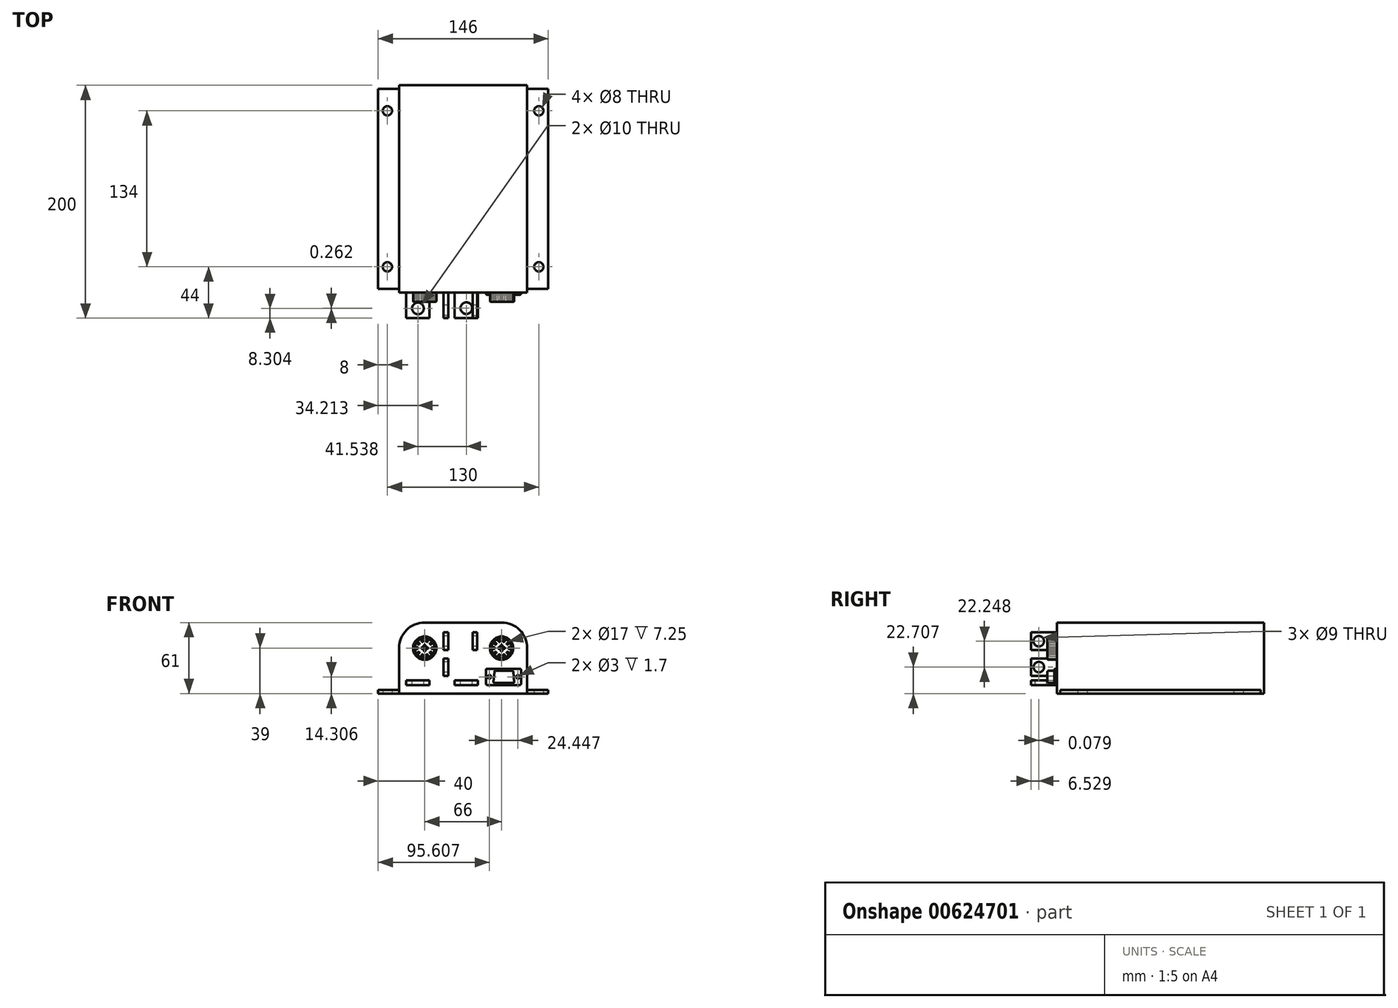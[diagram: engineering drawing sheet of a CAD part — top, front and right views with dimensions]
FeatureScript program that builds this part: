
annotation { "Feature Type Name" : "Feature", "Feature Type Description" : "" }
export const myFeature = defineFeature(function(context is Context, id is Id, definition is map)
    precondition{}
    {
        {
            var Q0;
            Q0=qCreatedBy(makeId("Top.planeOp"),FACE);
            var sketch = newSketch(context, id + "F0", { "sketchPlane" : qUnion([Q0])});
            skLineSegment(sketch, "E0.bottom", {"start": v(73, -86) * mm, "end": v(-73, -86) * mm});
            skLineSegment(sketch, "E0.top", {"start": v(73, 86) * mm, "end": v(-73, 86) * mm});
            skLineSegment(sketch, "E0.left", {"start": v(73, -86) * mm, "end": v(73, 86) * mm});
            skLineSegment(sketch, "E0.right", {"start": v(-73, -86) * mm, "end": v(-73, 86) * mm});
            skPoint(sketch, "E0.middle", {"position": v(0, 0) * mm});
            skLineSegment(sketch, "E1.bottom", {"start": v(65, -67) * mm, "end": v(-65, -67) * mm});
            skLineSegment(sketch, "E1.top", {"start": v(65, 67) * mm, "end": v(-65, 67) * mm});
            skLineSegment(sketch, "E1.left", {"start": v(65, -67) * mm, "end": v(65, 67) * mm});
            skLineSegment(sketch, "E1.right", {"start": v(-65, -67) * mm, "end": v(-65, 67) * mm});
            skLineSegment(sketch, "E2.bottom", {"start": v(55, -89) * mm, "end": v(-55, -89) * mm});
            skLineSegment(sketch, "E2.top", {"start": v(55, 89) * mm, "end": v(-55, 89) * mm});
            skLineSegment(sketch, "E2.left", {"start": v(55, -89) * mm, "end": v(55, 89) * mm});
            skLineSegment(sketch, "E2.right", {"start": v(-55, -89) * mm, "end": v(-55, 89) * mm});
            skCircle(sketch, "E3", {"center": v(-65, 67) * mm, "radius": 4 * mm});
            skCircle(sketch, "E4", {"center": v(65, 67) * mm, "radius": 4 * mm});
            skCircle(sketch, "E5", {"center": v(-65, -67) * mm, "radius": 4 * mm});
            skCircle(sketch, "E6", {"center": v(65, -67) * mm, "radius": 4 * mm});
            skSolve(sketch);
        }
        {
            var Q0;
            {var subQ5=sQuery(id+"F0.wireOp",EDGE,"E2.top");Q0=makeQuery(id+"F0.imprint","IMPRINT",FACE,{"disambiguationData":[TD([[makeQuery(id+"F0.imprint","IMPRINT",EDGE,{"derivedFrom":subQ5}),1.0]])]});}
            var Q1;
            {var subQ0=sQuery(id+"F0.wireOp",EDGE,"E2.left");var subQ1=sQuery(id+"F0.wireOp",EDGE,"E0.top");var subQ2=makeQuery(id+"F0.imprint","INTERSECT",VERTEX,{"derivedFrom":[subQ1,subQ0]});Q1=makeQuery(id+"F0.imprint","IMPRINT",FACE,{"disambiguationData":[TD([[makeQuery(id+"F0.imprint","IMPRINT",EDGE,{"disambiguationData":[TD([[subQ2,-1.0]])],"derivedFrom":subQ1}),1.0]])]});}
            var Q2;
            {var subQ0=sQuery(id+"F0.wireOp",EDGE,"E2.left");var subQ1=sQuery(id+"F0.wireOp",EDGE,"E1.bottom");var subQ2=makeQuery(id+"F0.imprint","INTERSECT",VERTEX,{"derivedFrom":[subQ1,subQ0]});Q2=makeQuery(id+"F0.imprint","IMPRINT",FACE,{"disambiguationData":[TD([[makeQuery(id+"F0.imprint","IMPRINT",EDGE,{"disambiguationData":[TD([[subQ2,-1.0]])],"derivedFrom":subQ1}),-1.0]])]});}
            var Q3;
            {var subQ0=sQuery(id+"F0.wireOp",EDGE,"E2.left");var subQ1=sQuery(id+"F0.wireOp",EDGE,"E0.bottom");var subQ2=makeQuery(id+"F0.imprint","INTERSECT",VERTEX,{"derivedFrom":[subQ1,subQ0]});Q3=makeQuery(id+"F0.imprint","IMPRINT",FACE,{"disambiguationData":[TD([[makeQuery(id+"F0.imprint","IMPRINT",EDGE,{"disambiguationData":[TD([[subQ2,-1.0]])],"derivedFrom":subQ1}),-1.0]])]});}
            var Q4;
            {var subQ5=sQuery(id+"F0.wireOp",EDGE,"E2.bottom");Q4=makeQuery(id+"F0.imprint","IMPRINT",FACE,{"disambiguationData":[TD([[makeQuery(id+"F0.imprint","IMPRINT",EDGE,{"derivedFrom":subQ5}),-1.0]])]});}
            extrude(context, id + "F1", {"entities" : qUnion([Q0, Q1, Q2, Q3, Q4]), "depth" : 61 * mm, "offsetDistance" : 25 * mm});
        }
        {
            var Q0;
            {var subQ9=sQuery(id+"F0.wireOp",EDGE,"E0.right");Q0=makeQuery(id+"F0.imprint","IMPRINT",FACE,{"disambiguationData":[TD([[makeQuery(id+"F0.imprint","IMPRINT",EDGE,{"derivedFrom":subQ9}),-1.0]])]});}
            var Q1;
            {var subQ0=sQuery(id+"F0.wireOp",EDGE,"E2.right");var subQ1=sQuery(id+"F0.wireOp",EDGE,"E1.bottom");var subQ2=makeQuery(id+"F0.imprint","INTERSECT",VERTEX,{"derivedFrom":[subQ1,subQ0]});Q1=makeQuery(id+"F0.imprint","IMPRINT",FACE,{"disambiguationData":[TD([[makeQuery(id+"F0.imprint","IMPRINT",EDGE,{"disambiguationData":[TD([[subQ2,-1.0]])],"derivedFrom":subQ1}),-1.0]])]});}
            var Q2;
            {var subQ5=sQuery(id+"F0.wireOp",EDGE,"E2.top");Q2=makeQuery(id+"F0.imprint","IMPRINT",FACE,{"disambiguationData":[TD([[makeQuery(id+"F0.imprint","IMPRINT",EDGE,{"derivedFrom":subQ5}),1.0]])]});}
            var Q3;
            {var subQ0=sQuery(id+"F0.wireOp",EDGE,"E2.left");var subQ1=sQuery(id+"F0.wireOp",EDGE,"E0.top");var subQ2=makeQuery(id+"F0.imprint","INTERSECT",VERTEX,{"derivedFrom":[subQ1,subQ0]});Q3=makeQuery(id+"F0.imprint","IMPRINT",FACE,{"disambiguationData":[TD([[makeQuery(id+"F0.imprint","IMPRINT",EDGE,{"disambiguationData":[TD([[subQ2,-1.0]])],"derivedFrom":subQ1}),1.0]])]});}
            var Q4;
            {var subQ0=sQuery(id+"F0.wireOp",EDGE,"E2.left");var subQ1=sQuery(id+"F0.wireOp",EDGE,"E1.bottom");var subQ2=makeQuery(id+"F0.imprint","INTERSECT",VERTEX,{"derivedFrom":[subQ1,subQ0]});Q4=makeQuery(id+"F0.imprint","IMPRINT",FACE,{"disambiguationData":[TD([[makeQuery(id+"F0.imprint","IMPRINT",EDGE,{"disambiguationData":[TD([[subQ2,-1.0]])],"derivedFrom":subQ1}),-1.0]])]});}
            var Q5;
            {var subQ0=sQuery(id+"F0.wireOp",EDGE,"E2.left");var subQ1=sQuery(id+"F0.wireOp",EDGE,"E0.bottom");var subQ2=makeQuery(id+"F0.imprint","INTERSECT",VERTEX,{"derivedFrom":[subQ1,subQ0]});Q5=makeQuery(id+"F0.imprint","IMPRINT",FACE,{"disambiguationData":[TD([[makeQuery(id+"F0.imprint","IMPRINT",EDGE,{"disambiguationData":[TD([[subQ2,-1.0]])],"derivedFrom":subQ1}),-1.0]])]});}
            var Q6;
            {var subQ5=sQuery(id+"F0.wireOp",EDGE,"E2.bottom");Q6=makeQuery(id+"F0.imprint","IMPRINT",FACE,{"disambiguationData":[TD([[makeQuery(id+"F0.imprint","IMPRINT",EDGE,{"derivedFrom":subQ5}),-1.0]])]});}
            var Q7;
            {var subQ1=sQuery(id+"F0.wireOp",EDGE,"E1.bottom");var subQ5=sQuery(id+"F0.wireOp",EDGE,"E6");var subQ11=makeQuery(id+"F0.imprint","INTERSECT",VERTEX,{"derivedFrom":[subQ1,subQ5]});Q7=makeQuery(id+"F0.imprint","IMPRINT",FACE,{"disambiguationData":[TD([[makeQuery(id+"F0.imprint","IMPRINT",EDGE,{"disambiguationData":[TD([[subQ11,-1.0]])],"derivedFrom":subQ1}),-1.0]])]});}
            var Q8;
            {var subQ5=sQuery(id+"F0.wireOp",EDGE,"E0.left");Q8=makeQuery(id+"F0.imprint","IMPRINT",FACE,{"disambiguationData":[TD([[makeQuery(id+"F0.imprint","IMPRINT",EDGE,{"derivedFrom":subQ5}),1.0]])]});}
            extrude(context, id + "F2", {"entities" : qUnion([Q0, Q1, Q2, Q3, Q4, Q5, Q6, Q7, Q8]), "operationType" : NewBodyOperationType.ADD, "depth" : 3 * mm, "offsetDistance" : 25 * mm});
        }
        {
            var Q0;
            Q0=makeQuery(id+"F1.opExtrude","CAP_EDGE",EDGE,{"disambiguationData":[OSD([sQuery(id+"F0.wireOp",EDGE,"E2.right")])],"isStart":false});
            var Q1;
            Q1=makeQuery(id+"F1.opExtrude","CAP_EDGE",EDGE,{"disambiguationData":[OSD([sQuery(id+"F0.wireOp",EDGE,"E2.left")])],"isStart":false});
            fillet(context, id + "F3", {"entities" : qUnion([Q0, Q1]), "radius" : 22 * mm, "tangentPropagation" : true, "allowEdgeOverflow" : false});
        }
        {
            var Q0;
            Q0=makeQuery(id+"F1.opExtrude","SWEPT_FACE",FACE,{"disambiguationData":[OSD([sQuery(id+"F0.wireOp",EDGE,"E2.bottom")])]});
            var sketch = newSketch(context, id + "F4", { "sketchPlane" : qUnion([Q0])});
            skCircle(sketch, "E7", {"center": v(33, 39) * mm, "radius": 10 * mm});
            skCircle(sketch, "E8", {"center": v(-33, 39) * mm, "radius": 10 * mm});
            skCircle(sketch, "E9", {"center": v(-33, 39) * mm, "radius": 8.5 * mm});
            skCircle(sketch, "E10", {"center": v(33, 39) * mm, "radius": 8.5 * mm});
            skCircle(sketch, "E11", {"center": v(-33, 39) * mm, "radius": 6.5 * mm});
            skCircle(sketch, "E12", {"center": v(33, 39) * mm, "radius": 6.5 * mm});
            skCircle(sketch, "E13.cCircle", {"center": v(-33, 39) * mm, "radius": 6.5 * mm, "construction": true});
            skLineSegment(sketch, "E13.0", {"start": v(-26.5, 39) * mm, "end": v(-27.74, 35.18) * mm});
            skLineSegment(sketch, "E13.1", {"start": v(-27.74, 35.18) * mm, "end": v(-31, 32.82) * mm});
            skLineSegment(sketch, "E13.2", {"start": v(-31, 32.82) * mm, "end": v(-35, 32.82) * mm});
            skLineSegment(sketch, "E13.3", {"start": v(-35, 32.82) * mm, "end": v(-38.26, 35.18) * mm});
            skLineSegment(sketch, "E13.4", {"start": v(-38.26, 35.18) * mm, "end": v(-39.5, 39) * mm});
            skLineSegment(sketch, "E13.5", {"start": v(-39.5, 39) * mm, "end": v(-38.26, 42.82) * mm});
            skLineSegment(sketch, "E13.6", {"start": v(-38.26, 42.82) * mm, "end": v(-35, 45.18) * mm});
            skLineSegment(sketch, "E13.7", {"start": v(-35, 45.18) * mm, "end": v(-31, 45.18) * mm});
            skLineSegment(sketch, "E13.8", {"start": v(-31, 45.18) * mm, "end": v(-27.74, 42.82) * mm});
            skLineSegment(sketch, "E13.9", {"start": v(-27.74, 42.82) * mm, "end": v(-26.5, 39) * mm});
            skCircle(sketch, "E14", {"center": v(-35, 45.18) * mm, "radius": 0.75 * mm});
            skCircle(sketch, "E15", {"center": v(-38.26, 42.82) * mm, "radius": 0.75 * mm});
            skCircle(sketch, "E16", {"center": v(-39.5, 39) * mm, "radius": 0.75 * mm});
            skCircle(sketch, "E17", {"center": v(-38.26, 35.18) * mm, "radius": 0.75 * mm});
            skCircle(sketch, "E18", {"center": v(-35, 32.82) * mm, "radius": 0.75 * mm});
            skCircle(sketch, "E19", {"center": v(-31, 32.82) * mm, "radius": 0.75 * mm});
            skCircle(sketch, "E20", {"center": v(-27.74, 35.18) * mm, "radius": 0.75 * mm});
            skCircle(sketch, "E21", {"center": v(-26.5, 39) * mm, "radius": 0.75 * mm});
            skCircle(sketch, "E22", {"center": v(-27.74, 42.82) * mm, "radius": 0.75 * mm});
            skCircle(sketch, "E23", {"center": v(-31, 45.18) * mm, "radius": 0.75 * mm});
            skCircle(sketch, "E24.cCircle", {"center": v(-33, 39) * mm, "radius": 2.12 * mm, "construction": true});
            skLineSegment(sketch, "E24.0", {"start": v(-30.88, 39) * mm, "end": v(-33, 36.88) * mm});
            skLineSegment(sketch, "E24.1", {"start": v(-33, 36.88) * mm, "end": v(-35.12, 39) * mm});
            skLineSegment(sketch, "E24.2", {"start": v(-35.12, 39) * mm, "end": v(-33, 41.12) * mm});
            skLineSegment(sketch, "E24.3", {"start": v(-33, 41.12) * mm, "end": v(-30.88, 39) * mm});
            skCircle(sketch, "E25", {"center": v(-33, 36.88) * mm, "radius": 0.75 * mm});
            skCircle(sketch, "E26", {"center": v(-33, 41.12) * mm, "radius": 0.75 * mm});
            skCircle(sketch, "E27", {"center": v(-30.88, 39) * mm, "radius": 0.75 * mm});
            skCircle(sketch, "E28", {"center": v(-35.12, 39) * mm, "radius": 0.75 * mm});
            skCircle(sketch, "E29.cCircle", {"center": v(33, 39) * mm, "radius": 6.5 * mm, "construction": true});
            skLineSegment(sketch, "E29.0", {"start": v(39.5, 39) * mm, "end": v(38.26, 35.18) * mm});
            skLineSegment(sketch, "E29.1", {"start": v(38.26, 35.18) * mm, "end": v(35, 32.82) * mm});
            skLineSegment(sketch, "E29.2", {"start": v(35, 32.82) * mm, "end": v(31, 32.82) * mm});
            skLineSegment(sketch, "E29.3", {"start": v(31, 32.82) * mm, "end": v(27.74, 35.18) * mm});
            skLineSegment(sketch, "E29.4", {"start": v(27.74, 35.18) * mm, "end": v(26.5, 39) * mm});
            skLineSegment(sketch, "E29.5", {"start": v(26.5, 39) * mm, "end": v(27.74, 42.82) * mm});
            skLineSegment(sketch, "E29.6", {"start": v(27.74, 42.82) * mm, "end": v(31, 45.18) * mm});
            skLineSegment(sketch, "E29.7", {"start": v(31, 45.18) * mm, "end": v(35, 45.18) * mm});
            skLineSegment(sketch, "E29.8", {"start": v(35, 45.18) * mm, "end": v(38.26, 42.82) * mm});
            skLineSegment(sketch, "E29.9", {"start": v(38.26, 42.82) * mm, "end": v(39.5, 39) * mm});
            skCircle(sketch, "E30", {"center": v(31, 45.18) * mm, "radius": 0.75 * mm});
            skCircle(sketch, "E31", {"center": v(27.74, 42.82) * mm, "radius": 0.75 * mm});
            skCircle(sketch, "E32", {"center": v(26.5, 39) * mm, "radius": 0.75 * mm});
            skCircle(sketch, "E33", {"center": v(27.74, 35.18) * mm, "radius": 0.75 * mm});
            skCircle(sketch, "E34", {"center": v(31, 32.82) * mm, "radius": 0.75 * mm});
            skCircle(sketch, "E35", {"center": v(35, 32.82) * mm, "radius": 0.75 * mm});
            skCircle(sketch, "E36", {"center": v(38.26, 35.18) * mm, "radius": 0.75 * mm});
            skCircle(sketch, "E37", {"center": v(39.5, 39) * mm, "radius": 0.75 * mm});
            skCircle(sketch, "E38", {"center": v(38.26, 42.82) * mm, "radius": 0.75 * mm});
            skCircle(sketch, "E39", {"center": v(35, 45.18) * mm, "radius": 0.75 * mm});
            skCircle(sketch, "E40.cCircle", {"center": v(33, 39) * mm, "radius": 2.12 * mm, "construction": true});
            skLineSegment(sketch, "E40.0", {"start": v(35.12, 39) * mm, "end": v(33, 36.88) * mm});
            skLineSegment(sketch, "E40.1", {"start": v(33, 36.88) * mm, "end": v(30.88, 39) * mm});
            skLineSegment(sketch, "E40.2", {"start": v(30.88, 39) * mm, "end": v(33, 41.12) * mm});
            skLineSegment(sketch, "E40.3", {"start": v(33, 41.12) * mm, "end": v(35.12, 39) * mm});
            skCircle(sketch, "E41", {"center": v(33, 36.88) * mm, "radius": 0.75 * mm});
            skCircle(sketch, "E42", {"center": v(33, 41.12) * mm, "radius": 0.75 * mm});
            skCircle(sketch, "E43", {"center": v(35.12, 39) * mm, "radius": 0.75 * mm});
            skCircle(sketch, "E44", {"center": v(30.88, 39) * mm, "radius": 0.75 * mm});
            skLineSegment(sketch, "E45.bottom", {"start": v(-48.79, 11.3) * mm, "end": v(-28.79, 11.3) * mm});
            skLineSegment(sketch, "E45.top", {"start": v(-48.79, 7.3) * mm, "end": v(-28.79, 7.3) * mm});
            skLineSegment(sketch, "E45.left", {"start": v(-48.79, 11.3) * mm, "end": v(-48.79, 7.3) * mm});
            skLineSegment(sketch, "E45.right", {"start": v(-28.79, 11.3) * mm, "end": v(-28.79, 7.3) * mm});
            skLineSegment(sketch, "E46.bottom", {"start": v(-16.77, 52.46) * mm, "end": v(-12.77, 52.46) * mm});
            skLineSegment(sketch, "E46.top", {"start": v(-16.77, 37.46) * mm, "end": v(-12.77, 37.46) * mm});
            skLineSegment(sketch, "E46.left", {"start": v(-16.77, 52.46) * mm, "end": v(-16.77, 37.46) * mm});
            skLineSegment(sketch, "E46.right", {"start": v(-12.77, 52.46) * mm, "end": v(-12.77, 37.46) * mm});
            skLineSegment(sketch, "E47.bottom", {"start": v(8.11, 52.46) * mm, "end": v(12.11, 52.46) * mm});
            skLineSegment(sketch, "E47.top", {"start": v(8.11, 37.46) * mm, "end": v(12.11, 37.46) * mm});
            skLineSegment(sketch, "E47.left", {"start": v(8.11, 52.46) * mm, "end": v(8.11, 37.46) * mm});
            skLineSegment(sketch, "E47.right", {"start": v(12.11, 52.46) * mm, "end": v(12.11, 37.46) * mm});
            skLineSegment(sketch, "E48.bottom", {"start": v(-16.77, 30.2) * mm, "end": v(-12.77, 30.2) * mm});
            skLineSegment(sketch, "E48.top", {"start": v(-16.77, 15.2) * mm, "end": v(-12.77, 15.2) * mm});
            skLineSegment(sketch, "E48.left", {"start": v(-16.77, 30.2) * mm, "end": v(-16.77, 15.2) * mm});
            skLineSegment(sketch, "E48.right", {"start": v(-12.77, 30.2) * mm, "end": v(-12.77, 15.2) * mm});
            skLineSegment(sketch, "E49.bottom", {"start": v(-7.25, 11.3) * mm, "end": v(12.75, 11.3) * mm});
            skLineSegment(sketch, "E49.top", {"start": v(-7.25, 7.3) * mm, "end": v(12.75, 7.3) * mm});
            skLineSegment(sketch, "E49.left", {"start": v(-7.25, 11.3) * mm, "end": v(-7.25, 7.3) * mm});
            skLineSegment(sketch, "E49.right", {"start": v(12.75, 11.3) * mm, "end": v(12.75, 7.3) * mm});
            skLineSegment(sketch, "E50.bottom", {"start": v(19.69, 7.3) * mm, "end": v(49.69, 7.3) * mm});
            skLineSegment(sketch, "E50.top", {"start": v(19.69, 21.3) * mm, "end": v(49.69, 21.3) * mm});
            skLineSegment(sketch, "E50.left", {"start": v(19.69, 7.3) * mm, "end": v(19.69, 21.3) * mm});
            skLineSegment(sketch, "E50.right", {"start": v(49.69, 7.3) * mm, "end": v(49.69, 21.3) * mm});
            skLineSegment(sketch, "E51", {"start": v(26.94, 19.6) * mm, "end": v(42.94, 19.6) * mm});
            skLineSegment(sketch, "E52", {"start": v(26.03, 9) * mm, "end": v(44.03, 9) * mm});
            skLineSegment(sketch, "E53", {"start": v(26.94, 19.6) * mm, "end": v(26.03, 9) * mm});
            skLineSegment(sketch, "E54", {"start": v(42.94, 19.6) * mm, "end": v(44.03, 9) * mm});
            skCircle(sketch, "E55", {"center": v(22.6, 14.3) * mm, "radius": 1.5 * mm});
            skPoint(sketch, "E55.centerSnap0", {"position": v(19.69, 14.3) * mm});
            skCircle(sketch, "E56", {"center": v(47.05, 14.3) * mm, "radius": 1.5 * mm});
            skPoint(sketch, "E56.centerSnap0", {"position": v(49.69, 14.3) * mm});
            skSolve(sketch);
        }
        {
            var Q0;
            {var subQ0=sQuery(id+"F4.wireOp",EDGE,"E11");var subQ2=sQuery(id+"F4.wireOp",EDGE,"E18");var subQ3=makeQuery(id+"F4.imprint","INTERSECT",VERTEX,{"disambiguationData":[OD(0.0)],"derivedFrom":[subQ0,subQ2]});Q0=makeQuery(id+"F4.imprint","IMPRINT",FACE,{"disambiguationData":[TD([[makeQuery(id+"F4.imprint","IMPRINT",EDGE,{"disambiguationData":[TD([[subQ3,-1.0]])],"derivedFrom":subQ2}),1.0]])]});}
            var Q1;
            {var subQ1=sQuery(id+"F4.wireOp",EDGE,"E13.2");var subQ3=sQuery(id+"F4.wireOp",EDGE,"E18");var subQ4=makeQuery(id+"F4.imprint","INTERSECT",VERTEX,{"derivedFrom":[subQ1,subQ3]});Q1=makeQuery(id+"F4.imprint","IMPRINT",FACE,{"disambiguationData":[TD([[makeQuery(id+"F4.imprint","IMPRINT",EDGE,{"disambiguationData":[TD([[subQ4,-1.0]])],"derivedFrom":subQ3}),1.0]])]});}
            var Q2;
            {var subQ0=sQuery(id+"F4.wireOp",EDGE,"E11");var subQ2=sQuery(id+"F4.wireOp",EDGE,"E19");var subQ3=makeQuery(id+"F4.imprint","INTERSECT",VERTEX,{"disambiguationData":[OD(0.0)],"derivedFrom":[subQ0,subQ2]});Q2=makeQuery(id+"F4.imprint","IMPRINT",FACE,{"disambiguationData":[TD([[makeQuery(id+"F4.imprint","IMPRINT",EDGE,{"disambiguationData":[TD([[subQ3,-1.0]])],"derivedFrom":subQ2}),1.0]])]});}
            var Q3;
            {var subQ1=sQuery(id+"F4.wireOp",EDGE,"E13.1");var subQ3=sQuery(id+"F4.wireOp",EDGE,"E19");var subQ4=makeQuery(id+"F4.imprint","INTERSECT",VERTEX,{"derivedFrom":[subQ1,subQ3]});Q3=makeQuery(id+"F4.imprint","IMPRINT",FACE,{"disambiguationData":[TD([[makeQuery(id+"F4.imprint","IMPRINT",EDGE,{"disambiguationData":[TD([[subQ4,-1.0]])],"derivedFrom":subQ3}),1.0]])]});}
            var Q4;
            {var subQ1=sQuery(id+"F4.wireOp",EDGE,"E11");var subQ3=sQuery(id+"F4.wireOp",EDGE,"E19");var subQ4=makeQuery(id+"F4.imprint","INTERSECT",VERTEX,{"disambiguationData":[OD(1.0)],"derivedFrom":[subQ1,subQ3]});Q4=makeQuery(id+"F4.imprint","IMPRINT",FACE,{"disambiguationData":[TD([[makeQuery(id+"F4.imprint","IMPRINT",EDGE,{"disambiguationData":[TD([[subQ4,-1.0]])],"derivedFrom":subQ3}),1.0]])]});}
            var Q5;
            {var subQ1=sQuery(id+"F4.wireOp",EDGE,"E11");var subQ3=sQuery(id+"F4.wireOp",EDGE,"E19");var subQ4=makeQuery(id+"F4.imprint","INTERSECT",VERTEX,{"disambiguationData":[OD(0.0)],"derivedFrom":[subQ1,subQ3]});Q5=makeQuery(id+"F4.imprint","IMPRINT",FACE,{"disambiguationData":[TD([[makeQuery(id+"F4.imprint","IMPRINT",EDGE,{"disambiguationData":[TD([[subQ4,1.0]])],"derivedFrom":subQ3}),1.0]])]});}
            var Q6;
            {var subQ0=sQuery(id+"F4.wireOp",EDGE,"E24.2");var subQ1=sQuery(id+"F4.wireOp",EDGE,"E24.1");var subQ2=makeQuery(id+"F4.imprint","INTERSECT",VERTEX,{"derivedFrom":[subQ1,subQ0]});Q6=makeQuery(id+"F4.imprint","IMPRINT",FACE,{"disambiguationData":[TD([[makeQuery(id+"F4.imprint","IMPRINT",EDGE,{"disambiguationData":[TD([[subQ2,1.0]])],"derivedFrom":subQ1}),-1.0]])]});}
            var Q7;
            {var subQ0=sQuery(id+"F4.wireOp",EDGE,"E24.2");var subQ1=sQuery(id+"F4.wireOp",EDGE,"E24.1");var subQ2=makeQuery(id+"F4.imprint","INTERSECT",VERTEX,{"derivedFrom":[subQ1,subQ0]});Q7=makeQuery(id+"F4.imprint","IMPRINT",FACE,{"disambiguationData":[TD([[makeQuery(id+"F4.imprint","IMPRINT",EDGE,{"disambiguationData":[TD([[subQ2,1.0]])],"derivedFrom":subQ1}),1.0]])]});}
            var Q8;
            {var subQ0=sQuery(id+"F4.wireOp",EDGE,"E24.3");var subQ1=sQuery(id+"F4.wireOp",EDGE,"E24.2");var subQ2=makeQuery(id+"F4.imprint","INTERSECT",VERTEX,{"derivedFrom":[subQ1,subQ0]});Q8=makeQuery(id+"F4.imprint","IMPRINT",FACE,{"disambiguationData":[TD([[makeQuery(id+"F4.imprint","IMPRINT",EDGE,{"disambiguationData":[TD([[subQ2,1.0]])],"derivedFrom":subQ1}),1.0]])]});}
            var Q9;
            {var subQ0=sQuery(id+"F4.wireOp",EDGE,"E24.3");var subQ1=sQuery(id+"F4.wireOp",EDGE,"E24.2");var subQ2=makeQuery(id+"F4.imprint","INTERSECT",VERTEX,{"derivedFrom":[subQ1,subQ0]});Q9=makeQuery(id+"F4.imprint","IMPRINT",FACE,{"disambiguationData":[TD([[makeQuery(id+"F4.imprint","IMPRINT",EDGE,{"disambiguationData":[TD([[subQ2,1.0]])],"derivedFrom":subQ1}),-1.0]])]});}
            var Q10;
            {var subQ0=sQuery(id+"F4.wireOp",EDGE,"E24.3");var subQ1=sQuery(id+"F4.wireOp",EDGE,"E24.0");var subQ2=makeQuery(id+"F4.imprint","INTERSECT",VERTEX,{"derivedFrom":[subQ1,subQ0]});Q10=makeQuery(id+"F4.imprint","IMPRINT",FACE,{"disambiguationData":[TD([[makeQuery(id+"F4.imprint","IMPRINT",EDGE,{"disambiguationData":[TD([[subQ2,-1.0]])],"derivedFrom":subQ1}),1.0]])]});}
            var Q11;
            {var subQ0=sQuery(id+"F4.wireOp",EDGE,"E24.3");var subQ1=sQuery(id+"F4.wireOp",EDGE,"E24.0");var subQ2=makeQuery(id+"F4.imprint","INTERSECT",VERTEX,{"derivedFrom":[subQ1,subQ0]});Q11=makeQuery(id+"F4.imprint","IMPRINT",FACE,{"disambiguationData":[TD([[makeQuery(id+"F4.imprint","IMPRINT",EDGE,{"disambiguationData":[TD([[subQ2,-1.0]])],"derivedFrom":subQ1}),-1.0]])]});}
            var Q12;
            {var subQ0=sQuery(id+"F4.wireOp",EDGE,"E24.1");var subQ1=sQuery(id+"F4.wireOp",EDGE,"E24.0");var subQ2=makeQuery(id+"F4.imprint","INTERSECT",VERTEX,{"derivedFrom":[subQ1,subQ0]});Q12=makeQuery(id+"F4.imprint","IMPRINT",FACE,{"disambiguationData":[TD([[makeQuery(id+"F4.imprint","IMPRINT",EDGE,{"disambiguationData":[TD([[subQ2,1.0]])],"derivedFrom":subQ1}),1.0]])]});}
            var Q13;
            {var subQ0=sQuery(id+"F4.wireOp",EDGE,"E24.1");var subQ1=sQuery(id+"F4.wireOp",EDGE,"E24.0");var subQ2=makeQuery(id+"F4.imprint","INTERSECT",VERTEX,{"derivedFrom":[subQ1,subQ0]});Q13=makeQuery(id+"F4.imprint","IMPRINT",FACE,{"disambiguationData":[TD([[makeQuery(id+"F4.imprint","IMPRINT",EDGE,{"disambiguationData":[TD([[subQ2,1.0]])],"derivedFrom":subQ1}),-1.0]])]});}
            var Q14;
            {var subQ1=sQuery(id+"F4.wireOp",EDGE,"E13.0");var subQ3=sQuery(id+"F4.wireOp",EDGE,"E20");var subQ4=makeQuery(id+"F4.imprint","INTERSECT",VERTEX,{"derivedFrom":[subQ1,subQ3]});Q14=makeQuery(id+"F4.imprint","IMPRINT",FACE,{"disambiguationData":[TD([[makeQuery(id+"F4.imprint","IMPRINT",EDGE,{"disambiguationData":[TD([[subQ4,-1.0]])],"derivedFrom":subQ3}),1.0]])]});}
            var Q15;
            {var subQ0=sQuery(id+"F4.wireOp",EDGE,"E11");var subQ2=sQuery(id+"F4.wireOp",EDGE,"E21");var subQ3=makeQuery(id+"F4.imprint","INTERSECT",VERTEX,{"disambiguationData":[OD(0.0)],"derivedFrom":[subQ0,subQ2]});Q15=makeQuery(id+"F4.imprint","IMPRINT",FACE,{"disambiguationData":[TD([[makeQuery(id+"F4.imprint","IMPRINT",EDGE,{"disambiguationData":[TD([[subQ3,1.0]])],"derivedFrom":subQ2}),1.0]])]});}
            var Q16;
            {var subQ1=sQuery(id+"F4.wireOp",EDGE,"E13.0");var subQ3=sQuery(id+"F4.wireOp",EDGE,"E21");var subQ4=makeQuery(id+"F4.imprint","INTERSECT",VERTEX,{"derivedFrom":[subQ1,subQ3]});Q16=makeQuery(id+"F4.imprint","IMPRINT",FACE,{"disambiguationData":[TD([[makeQuery(id+"F4.imprint","IMPRINT",EDGE,{"disambiguationData":[TD([[subQ4,1.0]])],"derivedFrom":subQ3}),1.0]])]});}
            var Q17;
            {var subQ0=sQuery(id+"F4.wireOp",EDGE,"E11");var subQ2=sQuery(id+"F4.wireOp",EDGE,"E22");var subQ3=makeQuery(id+"F4.imprint","INTERSECT",VERTEX,{"disambiguationData":[OD(0.0)],"derivedFrom":[subQ0,subQ2]});Q17=makeQuery(id+"F4.imprint","IMPRINT",FACE,{"disambiguationData":[TD([[makeQuery(id+"F4.imprint","IMPRINT",EDGE,{"disambiguationData":[TD([[subQ3,-1.0]])],"derivedFrom":subQ2}),1.0]])]});}
            var Q18;
            {var subQ1=sQuery(id+"F4.wireOp",EDGE,"E13.8");var subQ3=sQuery(id+"F4.wireOp",EDGE,"E22");var subQ4=makeQuery(id+"F4.imprint","INTERSECT",VERTEX,{"derivedFrom":[subQ1,subQ3]});Q18=makeQuery(id+"F4.imprint","IMPRINT",FACE,{"disambiguationData":[TD([[makeQuery(id+"F4.imprint","IMPRINT",EDGE,{"disambiguationData":[TD([[subQ4,-1.0]])],"derivedFrom":subQ3}),1.0]])]});}
            var Q19;
            {var subQ0=sQuery(id+"F4.wireOp",EDGE,"E11");var subQ2=sQuery(id+"F4.wireOp",EDGE,"E23");var subQ3=makeQuery(id+"F4.imprint","INTERSECT",VERTEX,{"disambiguationData":[OD(0.0)],"derivedFrom":[subQ0,subQ2]});Q19=makeQuery(id+"F4.imprint","IMPRINT",FACE,{"disambiguationData":[TD([[makeQuery(id+"F4.imprint","IMPRINT",EDGE,{"disambiguationData":[TD([[subQ3,-1.0]])],"derivedFrom":subQ2}),1.0]])]});}
            var Q20;
            {var subQ1=sQuery(id+"F4.wireOp",EDGE,"E13.7");var subQ3=sQuery(id+"F4.wireOp",EDGE,"E23");var subQ4=makeQuery(id+"F4.imprint","INTERSECT",VERTEX,{"derivedFrom":[subQ1,subQ3]});Q20=makeQuery(id+"F4.imprint","IMPRINT",FACE,{"disambiguationData":[TD([[makeQuery(id+"F4.imprint","IMPRINT",EDGE,{"disambiguationData":[TD([[subQ4,-1.0]])],"derivedFrom":subQ3}),1.0]])]});}
            var Q21;
            {var subQ0=sQuery(id+"F4.wireOp",EDGE,"E11");var subQ2=sQuery(id+"F4.wireOp",EDGE,"E14");var subQ3=makeQuery(id+"F4.imprint","INTERSECT",VERTEX,{"disambiguationData":[OD(0.0)],"derivedFrom":[subQ0,subQ2]});Q21=makeQuery(id+"F4.imprint","IMPRINT",FACE,{"disambiguationData":[TD([[makeQuery(id+"F4.imprint","IMPRINT",EDGE,{"disambiguationData":[TD([[subQ3,-1.0]])],"derivedFrom":subQ2}),1.0]])]});}
            var Q22;
            {var subQ1=sQuery(id+"F4.wireOp",EDGE,"E13.6");var subQ3=sQuery(id+"F4.wireOp",EDGE,"E14");var subQ4=makeQuery(id+"F4.imprint","INTERSECT",VERTEX,{"derivedFrom":[subQ1,subQ3]});Q22=makeQuery(id+"F4.imprint","IMPRINT",FACE,{"disambiguationData":[TD([[makeQuery(id+"F4.imprint","IMPRINT",EDGE,{"disambiguationData":[TD([[subQ4,-1.0]])],"derivedFrom":subQ3}),1.0]])]});}
            var Q23;
            {var subQ0=sQuery(id+"F4.wireOp",EDGE,"E11");var subQ2=sQuery(id+"F4.wireOp",EDGE,"E15");var subQ3=makeQuery(id+"F4.imprint","INTERSECT",VERTEX,{"disambiguationData":[OD(0.0)],"derivedFrom":[subQ0,subQ2]});Q23=makeQuery(id+"F4.imprint","IMPRINT",FACE,{"disambiguationData":[TD([[makeQuery(id+"F4.imprint","IMPRINT",EDGE,{"disambiguationData":[TD([[subQ3,-1.0]])],"derivedFrom":subQ2}),1.0]])]});}
            var Q24;
            {var subQ1=sQuery(id+"F4.wireOp",EDGE,"E13.5");var subQ3=sQuery(id+"F4.wireOp",EDGE,"E15");var subQ4=makeQuery(id+"F4.imprint","INTERSECT",VERTEX,{"derivedFrom":[subQ1,subQ3]});Q24=makeQuery(id+"F4.imprint","IMPRINT",FACE,{"disambiguationData":[TD([[makeQuery(id+"F4.imprint","IMPRINT",EDGE,{"disambiguationData":[TD([[subQ4,-1.0]])],"derivedFrom":subQ3}),1.0]])]});}
            var Q25;
            {var subQ0=sQuery(id+"F4.wireOp",EDGE,"E11");var subQ2=sQuery(id+"F4.wireOp",EDGE,"E16");var subQ3=makeQuery(id+"F4.imprint","INTERSECT",VERTEX,{"disambiguationData":[OD(0.0)],"derivedFrom":[subQ0,subQ2]});Q25=makeQuery(id+"F4.imprint","IMPRINT",FACE,{"disambiguationData":[TD([[makeQuery(id+"F4.imprint","IMPRINT",EDGE,{"disambiguationData":[TD([[subQ3,-1.0]])],"derivedFrom":subQ2}),1.0]])]});}
            var Q26;
            {var subQ0=sQuery(id+"F4.wireOp",EDGE,"E11");var subQ2=sQuery(id+"F4.wireOp",EDGE,"E17");var subQ3=makeQuery(id+"F4.imprint","INTERSECT",VERTEX,{"disambiguationData":[OD(0.0)],"derivedFrom":[subQ0,subQ2]});Q26=makeQuery(id+"F4.imprint","IMPRINT",FACE,{"disambiguationData":[TD([[makeQuery(id+"F4.imprint","IMPRINT",EDGE,{"disambiguationData":[TD([[subQ3,-1.0]])],"derivedFrom":subQ2}),1.0]])]});}
            var Q27;
            {var subQ1=sQuery(id+"F4.wireOp",EDGE,"E13.3");var subQ3=sQuery(id+"F4.wireOp",EDGE,"E17");var subQ4=makeQuery(id+"F4.imprint","INTERSECT",VERTEX,{"derivedFrom":[subQ1,subQ3]});Q27=makeQuery(id+"F4.imprint","IMPRINT",FACE,{"disambiguationData":[TD([[makeQuery(id+"F4.imprint","IMPRINT",EDGE,{"disambiguationData":[TD([[subQ4,-1.0]])],"derivedFrom":subQ3}),1.0]])]});}
            var Q28;
            {var subQ1=sQuery(id+"F4.wireOp",EDGE,"E11");var subQ3=sQuery(id+"F4.wireOp",EDGE,"E14");var subQ4=makeQuery(id+"F4.imprint","INTERSECT",VERTEX,{"disambiguationData":[OD(0.0)],"derivedFrom":[subQ1,subQ3]});Q28=makeQuery(id+"F4.imprint","IMPRINT",FACE,{"disambiguationData":[TD([[makeQuery(id+"F4.imprint","IMPRINT",EDGE,{"disambiguationData":[TD([[subQ4,1.0]])],"derivedFrom":subQ3}),1.0]])]});}
            var Q29;
            {var subQ1=sQuery(id+"F4.wireOp",EDGE,"E11");var subQ3=sQuery(id+"F4.wireOp",EDGE,"E14");var subQ4=makeQuery(id+"F4.imprint","INTERSECT",VERTEX,{"disambiguationData":[OD(1.0)],"derivedFrom":[subQ1,subQ3]});Q29=makeQuery(id+"F4.imprint","IMPRINT",FACE,{"disambiguationData":[TD([[makeQuery(id+"F4.imprint","IMPRINT",EDGE,{"disambiguationData":[TD([[subQ4,-1.0]])],"derivedFrom":subQ3}),1.0]])]});}
            var Q30;
            {var subQ1=sQuery(id+"F4.wireOp",EDGE,"E11");var subQ3=sQuery(id+"F4.wireOp",EDGE,"E15");var subQ4=makeQuery(id+"F4.imprint","INTERSECT",VERTEX,{"disambiguationData":[OD(0.0)],"derivedFrom":[subQ1,subQ3]});Q30=makeQuery(id+"F4.imprint","IMPRINT",FACE,{"disambiguationData":[TD([[makeQuery(id+"F4.imprint","IMPRINT",EDGE,{"disambiguationData":[TD([[subQ4,1.0]])],"derivedFrom":subQ3}),1.0]])]});}
            var Q31;
            {var subQ1=sQuery(id+"F4.wireOp",EDGE,"E11");var subQ3=sQuery(id+"F4.wireOp",EDGE,"E16");var subQ4=makeQuery(id+"F4.imprint","INTERSECT",VERTEX,{"disambiguationData":[OD(0.0)],"derivedFrom":[subQ1,subQ3]});Q31=makeQuery(id+"F4.imprint","IMPRINT",FACE,{"disambiguationData":[TD([[makeQuery(id+"F4.imprint","IMPRINT",EDGE,{"disambiguationData":[TD([[subQ4,1.0]])],"derivedFrom":subQ3}),1.0]])]});}
            var Q32;
            {var subQ1=sQuery(id+"F4.wireOp",EDGE,"E11");var subQ3=sQuery(id+"F4.wireOp",EDGE,"E15");var subQ4=makeQuery(id+"F4.imprint","INTERSECT",VERTEX,{"disambiguationData":[OD(1.0)],"derivedFrom":[subQ1,subQ3]});Q32=makeQuery(id+"F4.imprint","IMPRINT",FACE,{"disambiguationData":[TD([[makeQuery(id+"F4.imprint","IMPRINT",EDGE,{"disambiguationData":[TD([[subQ4,-1.0]])],"derivedFrom":subQ3}),1.0]])]});}
            var Q33;
            {var subQ1=sQuery(id+"F4.wireOp",EDGE,"E11");var subQ3=sQuery(id+"F4.wireOp",EDGE,"E23");var subQ4=makeQuery(id+"F4.imprint","INTERSECT",VERTEX,{"disambiguationData":[OD(1.0)],"derivedFrom":[subQ1,subQ3]});Q33=makeQuery(id+"F4.imprint","IMPRINT",FACE,{"disambiguationData":[TD([[makeQuery(id+"F4.imprint","IMPRINT",EDGE,{"disambiguationData":[TD([[subQ4,-1.0]])],"derivedFrom":subQ3}),1.0]])]});}
            var Q34;
            {var subQ1=sQuery(id+"F4.wireOp",EDGE,"E11");var subQ3=sQuery(id+"F4.wireOp",EDGE,"E23");var subQ4=makeQuery(id+"F4.imprint","INTERSECT",VERTEX,{"disambiguationData":[OD(0.0)],"derivedFrom":[subQ1,subQ3]});Q34=makeQuery(id+"F4.imprint","IMPRINT",FACE,{"disambiguationData":[TD([[makeQuery(id+"F4.imprint","IMPRINT",EDGE,{"disambiguationData":[TD([[subQ4,1.0]])],"derivedFrom":subQ3}),1.0]])]});}
            var Q35;
            {var subQ1=sQuery(id+"F4.wireOp",EDGE,"E11");var subQ3=sQuery(id+"F4.wireOp",EDGE,"E22");var subQ4=makeQuery(id+"F4.imprint","INTERSECT",VERTEX,{"disambiguationData":[OD(1.0)],"derivedFrom":[subQ1,subQ3]});Q35=makeQuery(id+"F4.imprint","IMPRINT",FACE,{"disambiguationData":[TD([[makeQuery(id+"F4.imprint","IMPRINT",EDGE,{"disambiguationData":[TD([[subQ4,-1.0]])],"derivedFrom":subQ3}),1.0]])]});}
            var Q36;
            {var subQ1=sQuery(id+"F4.wireOp",EDGE,"E11");var subQ3=sQuery(id+"F4.wireOp",EDGE,"E22");var subQ4=makeQuery(id+"F4.imprint","INTERSECT",VERTEX,{"disambiguationData":[OD(0.0)],"derivedFrom":[subQ1,subQ3]});Q36=makeQuery(id+"F4.imprint","IMPRINT",FACE,{"disambiguationData":[TD([[makeQuery(id+"F4.imprint","IMPRINT",EDGE,{"disambiguationData":[TD([[subQ4,1.0]])],"derivedFrom":subQ3}),1.0]])]});}
            var Q37;
            {var subQ1=sQuery(id+"F4.wireOp",EDGE,"E11");var subQ3=sQuery(id+"F4.wireOp",EDGE,"E21");var subQ4=makeQuery(id+"F4.imprint","INTERSECT",VERTEX,{"disambiguationData":[OD(0.0)],"derivedFrom":[subQ1,subQ3]});Q37=makeQuery(id+"F4.imprint","IMPRINT",FACE,{"disambiguationData":[TD([[makeQuery(id+"F4.imprint","IMPRINT",EDGE,{"disambiguationData":[TD([[subQ4,-1.0]])],"derivedFrom":subQ3}),1.0]])]});}
            var Q38;
            {var subQ0=sQuery(id+"F4.wireOp",EDGE,"E11");var subQ2=sQuery(id+"F4.wireOp",EDGE,"E20");var subQ3=makeQuery(id+"F4.imprint","INTERSECT",VERTEX,{"disambiguationData":[OD(0.0)],"derivedFrom":[subQ0,subQ2]});Q38=makeQuery(id+"F4.imprint","IMPRINT",FACE,{"disambiguationData":[TD([[makeQuery(id+"F4.imprint","IMPRINT",EDGE,{"disambiguationData":[TD([[subQ3,-1.0]])],"derivedFrom":subQ2}),1.0]])]});}
            var Q39;
            {var subQ1=sQuery(id+"F4.wireOp",EDGE,"E11");var subQ3=sQuery(id+"F4.wireOp",EDGE,"E17");var subQ4=makeQuery(id+"F4.imprint","INTERSECT",VERTEX,{"disambiguationData":[OD(1.0)],"derivedFrom":[subQ1,subQ3]});Q39=makeQuery(id+"F4.imprint","IMPRINT",FACE,{"disambiguationData":[TD([[makeQuery(id+"F4.imprint","IMPRINT",EDGE,{"disambiguationData":[TD([[subQ4,-1.0]])],"derivedFrom":subQ3}),1.0]])]});}
            var Q40;
            {var subQ1=sQuery(id+"F4.wireOp",EDGE,"E11");var subQ3=sQuery(id+"F4.wireOp",EDGE,"E18");var subQ4=makeQuery(id+"F4.imprint","INTERSECT",VERTEX,{"disambiguationData":[OD(1.0)],"derivedFrom":[subQ1,subQ3]});Q40=makeQuery(id+"F4.imprint","IMPRINT",FACE,{"disambiguationData":[TD([[makeQuery(id+"F4.imprint","IMPRINT",EDGE,{"disambiguationData":[TD([[subQ4,-1.0]])],"derivedFrom":subQ3}),1.0]])]});}
            var Q41;
            {var subQ1=sQuery(id+"F4.wireOp",EDGE,"E11");var subQ3=sQuery(id+"F4.wireOp",EDGE,"E18");var subQ4=makeQuery(id+"F4.imprint","INTERSECT",VERTEX,{"disambiguationData":[OD(0.0)],"derivedFrom":[subQ1,subQ3]});Q41=makeQuery(id+"F4.imprint","IMPRINT",FACE,{"disambiguationData":[TD([[makeQuery(id+"F4.imprint","IMPRINT",EDGE,{"disambiguationData":[TD([[subQ4,1.0]])],"derivedFrom":subQ3}),1.0]])]});}
            var Q42;
            {var subQ1=sQuery(id+"F4.wireOp",EDGE,"E11");var subQ3=sQuery(id+"F4.wireOp",EDGE,"E20");var subQ4=makeQuery(id+"F4.imprint","INTERSECT",VERTEX,{"disambiguationData":[OD(0.0)],"derivedFrom":[subQ1,subQ3]});Q42=makeQuery(id+"F4.imprint","IMPRINT",FACE,{"disambiguationData":[TD([[makeQuery(id+"F4.imprint","IMPRINT",EDGE,{"disambiguationData":[TD([[subQ4,1.0]])],"derivedFrom":subQ3}),1.0]])]});}
            var Q43;
            {var subQ1=sQuery(id+"F4.wireOp",EDGE,"E11");var subQ3=sQuery(id+"F4.wireOp",EDGE,"E20");var subQ4=makeQuery(id+"F4.imprint","INTERSECT",VERTEX,{"disambiguationData":[OD(1.0)],"derivedFrom":[subQ1,subQ3]});Q43=makeQuery(id+"F4.imprint","IMPRINT",FACE,{"disambiguationData":[TD([[makeQuery(id+"F4.imprint","IMPRINT",EDGE,{"disambiguationData":[TD([[subQ4,-1.0]])],"derivedFrom":subQ3}),1.0]])]});}
            var Q44;
            {var subQ1=sQuery(id+"F4.wireOp",EDGE,"E11");var subQ3=sQuery(id+"F4.wireOp",EDGE,"E21");var subQ4=makeQuery(id+"F4.imprint","INTERSECT",VERTEX,{"disambiguationData":[OD(1.0)],"derivedFrom":[subQ1,subQ3]});Q44=makeQuery(id+"F4.imprint","IMPRINT",FACE,{"disambiguationData":[TD([[makeQuery(id+"F4.imprint","IMPRINT",EDGE,{"disambiguationData":[TD([[subQ4,1.0]])],"derivedFrom":subQ3}),1.0]])]});}
            var Q45;
            {var subQ1=sQuery(id+"F4.wireOp",EDGE,"E11");var subQ3=sQuery(id+"F4.wireOp",EDGE,"E17");var subQ4=makeQuery(id+"F4.imprint","INTERSECT",VERTEX,{"disambiguationData":[OD(0.0)],"derivedFrom":[subQ1,subQ3]});Q45=makeQuery(id+"F4.imprint","IMPRINT",FACE,{"disambiguationData":[TD([[makeQuery(id+"F4.imprint","IMPRINT",EDGE,{"disambiguationData":[TD([[subQ4,1.0]])],"derivedFrom":subQ3}),1.0]])]});}
            var Q46;
            {var subQ1=sQuery(id+"F4.wireOp",EDGE,"E11");var subQ3=sQuery(id+"F4.wireOp",EDGE,"E16");var subQ4=makeQuery(id+"F4.imprint","INTERSECT",VERTEX,{"disambiguationData":[OD(1.0)],"derivedFrom":[subQ1,subQ3]});Q46=makeQuery(id+"F4.imprint","IMPRINT",FACE,{"disambiguationData":[TD([[makeQuery(id+"F4.imprint","IMPRINT",EDGE,{"disambiguationData":[TD([[subQ4,-1.0]])],"derivedFrom":subQ3}),1.0]])]});}
            var Q47;
            {var subQ1=sQuery(id+"F4.wireOp",EDGE,"E13.4");var subQ3=sQuery(id+"F4.wireOp",EDGE,"E16");var subQ4=makeQuery(id+"F4.imprint","INTERSECT",VERTEX,{"derivedFrom":[subQ1,subQ3]});Q47=makeQuery(id+"F4.imprint","IMPRINT",FACE,{"disambiguationData":[TD([[makeQuery(id+"F4.imprint","IMPRINT",EDGE,{"disambiguationData":[TD([[subQ4,-1.0]])],"derivedFrom":subQ3}),1.0]])]});}
            var Q48;
            {var subQ0=sQuery(id+"F4.wireOp",EDGE,"E40.1");var subQ1=sQuery(id+"F4.wireOp",EDGE,"E40.0");var subQ2=makeQuery(id+"F4.imprint","INTERSECT",VERTEX,{"derivedFrom":[subQ1,subQ0]});Q48=makeQuery(id+"F4.imprint","IMPRINT",FACE,{"disambiguationData":[TD([[makeQuery(id+"F4.imprint","IMPRINT",EDGE,{"disambiguationData":[TD([[subQ2,1.0]])],"derivedFrom":subQ1}),1.0]])]});}
            var Q49;
            {var subQ0=sQuery(id+"F4.wireOp",EDGE,"E40.1");var subQ1=sQuery(id+"F4.wireOp",EDGE,"E40.0");var subQ2=makeQuery(id+"F4.imprint","INTERSECT",VERTEX,{"derivedFrom":[subQ1,subQ0]});Q49=makeQuery(id+"F4.imprint","IMPRINT",FACE,{"disambiguationData":[TD([[makeQuery(id+"F4.imprint","IMPRINT",EDGE,{"disambiguationData":[TD([[subQ2,1.0]])],"derivedFrom":subQ1}),-1.0]])]});}
            var Q50;
            {var subQ0=sQuery(id+"F4.wireOp",EDGE,"E40.3");var subQ1=sQuery(id+"F4.wireOp",EDGE,"E40.0");var subQ2=makeQuery(id+"F4.imprint","INTERSECT",VERTEX,{"derivedFrom":[subQ1,subQ0]});Q50=makeQuery(id+"F4.imprint","IMPRINT",FACE,{"disambiguationData":[TD([[makeQuery(id+"F4.imprint","IMPRINT",EDGE,{"disambiguationData":[TD([[subQ2,-1.0]])],"derivedFrom":subQ1}),1.0]])]});}
            var Q51;
            {var subQ0=sQuery(id+"F4.wireOp",EDGE,"E40.3");var subQ1=sQuery(id+"F4.wireOp",EDGE,"E40.0");var subQ2=makeQuery(id+"F4.imprint","INTERSECT",VERTEX,{"derivedFrom":[subQ1,subQ0]});Q51=makeQuery(id+"F4.imprint","IMPRINT",FACE,{"disambiguationData":[TD([[makeQuery(id+"F4.imprint","IMPRINT",EDGE,{"disambiguationData":[TD([[subQ2,-1.0]])],"derivedFrom":subQ1}),-1.0]])]});}
            var Q52;
            {var subQ0=sQuery(id+"F4.wireOp",EDGE,"E40.3");var subQ1=sQuery(id+"F4.wireOp",EDGE,"E40.2");var subQ2=makeQuery(id+"F4.imprint","INTERSECT",VERTEX,{"derivedFrom":[subQ1,subQ0]});Q52=makeQuery(id+"F4.imprint","IMPRINT",FACE,{"disambiguationData":[TD([[makeQuery(id+"F4.imprint","IMPRINT",EDGE,{"disambiguationData":[TD([[subQ2,1.0]])],"derivedFrom":subQ1}),1.0]])]});}
            var Q53;
            {var subQ0=sQuery(id+"F4.wireOp",EDGE,"E40.3");var subQ1=sQuery(id+"F4.wireOp",EDGE,"E40.2");var subQ2=makeQuery(id+"F4.imprint","INTERSECT",VERTEX,{"derivedFrom":[subQ1,subQ0]});Q53=makeQuery(id+"F4.imprint","IMPRINT",FACE,{"disambiguationData":[TD([[makeQuery(id+"F4.imprint","IMPRINT",EDGE,{"disambiguationData":[TD([[subQ2,1.0]])],"derivedFrom":subQ1}),-1.0]])]});}
            var Q54;
            {var subQ0=sQuery(id+"F4.wireOp",EDGE,"E40.2");var subQ1=sQuery(id+"F4.wireOp",EDGE,"E40.1");var subQ2=makeQuery(id+"F4.imprint","INTERSECT",VERTEX,{"derivedFrom":[subQ1,subQ0]});Q54=makeQuery(id+"F4.imprint","IMPRINT",FACE,{"disambiguationData":[TD([[makeQuery(id+"F4.imprint","IMPRINT",EDGE,{"disambiguationData":[TD([[subQ2,1.0]])],"derivedFrom":subQ1}),1.0]])]});}
            var Q55;
            {var subQ0=sQuery(id+"F4.wireOp",EDGE,"E40.2");var subQ1=sQuery(id+"F4.wireOp",EDGE,"E40.1");var subQ2=makeQuery(id+"F4.imprint","INTERSECT",VERTEX,{"derivedFrom":[subQ1,subQ0]});Q55=makeQuery(id+"F4.imprint","IMPRINT",FACE,{"disambiguationData":[TD([[makeQuery(id+"F4.imprint","IMPRINT",EDGE,{"disambiguationData":[TD([[subQ2,1.0]])],"derivedFrom":subQ1}),-1.0]])]});}
            var Q56;
            {var subQ0=sQuery(id+"F4.wireOp",EDGE,"E12");var subQ2=sQuery(id+"F4.wireOp",EDGE,"E35");var subQ3=makeQuery(id+"F4.imprint","INTERSECT",VERTEX,{"disambiguationData":[OD(0.0)],"derivedFrom":[subQ0,subQ2]});Q56=makeQuery(id+"F4.imprint","IMPRINT",FACE,{"disambiguationData":[TD([[makeQuery(id+"F4.imprint","IMPRINT",EDGE,{"disambiguationData":[TD([[subQ3,-1.0]])],"derivedFrom":subQ2}),1.0]])]});}
            var Q57;
            {var subQ1=sQuery(id+"F4.wireOp",EDGE,"E29.1");var subQ3=sQuery(id+"F4.wireOp",EDGE,"E35");var subQ4=makeQuery(id+"F4.imprint","INTERSECT",VERTEX,{"derivedFrom":[subQ1,subQ3]});Q57=makeQuery(id+"F4.imprint","IMPRINT",FACE,{"disambiguationData":[TD([[makeQuery(id+"F4.imprint","IMPRINT",EDGE,{"disambiguationData":[TD([[subQ4,-1.0]])],"derivedFrom":subQ3}),1.0]])]});}
            var Q58;
            {var subQ1=sQuery(id+"F4.wireOp",EDGE,"E12");var subQ3=sQuery(id+"F4.wireOp",EDGE,"E35");var subQ4=makeQuery(id+"F4.imprint","INTERSECT",VERTEX,{"disambiguationData":[OD(1.0)],"derivedFrom":[subQ1,subQ3]});Q58=makeQuery(id+"F4.imprint","IMPRINT",FACE,{"disambiguationData":[TD([[makeQuery(id+"F4.imprint","IMPRINT",EDGE,{"disambiguationData":[TD([[subQ4,-1.0]])],"derivedFrom":subQ3}),1.0]])]});}
            var Q59;
            {var subQ1=sQuery(id+"F4.wireOp",EDGE,"E12");var subQ3=sQuery(id+"F4.wireOp",EDGE,"E35");var subQ4=makeQuery(id+"F4.imprint","INTERSECT",VERTEX,{"disambiguationData":[OD(0.0)],"derivedFrom":[subQ1,subQ3]});Q59=makeQuery(id+"F4.imprint","IMPRINT",FACE,{"disambiguationData":[TD([[makeQuery(id+"F4.imprint","IMPRINT",EDGE,{"disambiguationData":[TD([[subQ4,1.0]])],"derivedFrom":subQ3}),1.0]])]});}
            var Q60;
            {var subQ0=sQuery(id+"F4.wireOp",EDGE,"E12");var subQ2=sQuery(id+"F4.wireOp",EDGE,"E34");var subQ3=makeQuery(id+"F4.imprint","INTERSECT",VERTEX,{"disambiguationData":[OD(0.0)],"derivedFrom":[subQ0,subQ2]});Q60=makeQuery(id+"F4.imprint","IMPRINT",FACE,{"disambiguationData":[TD([[makeQuery(id+"F4.imprint","IMPRINT",EDGE,{"disambiguationData":[TD([[subQ3,-1.0]])],"derivedFrom":subQ2}),1.0]])]});}
            var Q61;
            {var subQ0=sQuery(id+"F4.wireOp",EDGE,"E12");var subQ2=sQuery(id+"F4.wireOp",EDGE,"E34");var subQ3=makeQuery(id+"F4.imprint","INTERSECT",VERTEX,{"disambiguationData":[OD(0.0)],"derivedFrom":[subQ0,subQ2]});Q61=makeQuery(id+"F4.imprint","IMPRINT",FACE,{"disambiguationData":[TD([[makeQuery(id+"F4.imprint","IMPRINT",EDGE,{"disambiguationData":[TD([[subQ3,-1.0]])],"derivedFrom":subQ2}),1.0]])]});}
            var Q62;
            {var subQ1=sQuery(id+"F4.wireOp",EDGE,"E29.2");var subQ3=sQuery(id+"F4.wireOp",EDGE,"E34");var subQ4=makeQuery(id+"F4.imprint","INTERSECT",VERTEX,{"derivedFrom":[subQ1,subQ3]});Q62=makeQuery(id+"F4.imprint","IMPRINT",FACE,{"disambiguationData":[TD([[makeQuery(id+"F4.imprint","IMPRINT",EDGE,{"disambiguationData":[TD([[subQ4,-1.0]])],"derivedFrom":subQ3}),1.0]])]});}
            var Q63;
            {var subQ1=sQuery(id+"F4.wireOp",EDGE,"E12");var subQ3=sQuery(id+"F4.wireOp",EDGE,"E34");var subQ4=makeQuery(id+"F4.imprint","INTERSECT",VERTEX,{"disambiguationData":[OD(0.0)],"derivedFrom":[subQ1,subQ3]});Q63=makeQuery(id+"F4.imprint","IMPRINT",FACE,{"disambiguationData":[TD([[makeQuery(id+"F4.imprint","IMPRINT",EDGE,{"disambiguationData":[TD([[subQ4,1.0]])],"derivedFrom":subQ3}),1.0]])]});}
            var Q64;
            {var subQ0=sQuery(id+"F4.wireOp",EDGE,"E12");var subQ2=sQuery(id+"F4.wireOp",EDGE,"E33");var subQ3=makeQuery(id+"F4.imprint","INTERSECT",VERTEX,{"disambiguationData":[OD(0.0)],"derivedFrom":[subQ0,subQ2]});Q64=makeQuery(id+"F4.imprint","IMPRINT",FACE,{"disambiguationData":[TD([[makeQuery(id+"F4.imprint","IMPRINT",EDGE,{"disambiguationData":[TD([[subQ3,-1.0]])],"derivedFrom":subQ2}),1.0]])]});}
            var Q65;
            {var subQ1=sQuery(id+"F4.wireOp",EDGE,"E29.3");var subQ3=sQuery(id+"F4.wireOp",EDGE,"E33");var subQ4=makeQuery(id+"F4.imprint","INTERSECT",VERTEX,{"derivedFrom":[subQ1,subQ3]});Q65=makeQuery(id+"F4.imprint","IMPRINT",FACE,{"disambiguationData":[TD([[makeQuery(id+"F4.imprint","IMPRINT",EDGE,{"disambiguationData":[TD([[subQ4,-1.0]])],"derivedFrom":subQ3}),1.0]])]});}
            var Q66;
            {var subQ1=sQuery(id+"F4.wireOp",EDGE,"E12");var subQ3=sQuery(id+"F4.wireOp",EDGE,"E33");var subQ4=makeQuery(id+"F4.imprint","INTERSECT",VERTEX,{"disambiguationData":[OD(0.0)],"derivedFrom":[subQ1,subQ3]});Q66=makeQuery(id+"F4.imprint","IMPRINT",FACE,{"disambiguationData":[TD([[makeQuery(id+"F4.imprint","IMPRINT",EDGE,{"disambiguationData":[TD([[subQ4,1.0]])],"derivedFrom":subQ3}),1.0]])]});}
            var Q67;
            {var subQ1=sQuery(id+"F4.wireOp",EDGE,"E12");var subQ3=sQuery(id+"F4.wireOp",EDGE,"E33");var subQ4=makeQuery(id+"F4.imprint","INTERSECT",VERTEX,{"disambiguationData":[OD(1.0)],"derivedFrom":[subQ1,subQ3]});Q67=makeQuery(id+"F4.imprint","IMPRINT",FACE,{"disambiguationData":[TD([[makeQuery(id+"F4.imprint","IMPRINT",EDGE,{"disambiguationData":[TD([[subQ4,-1.0]])],"derivedFrom":subQ3}),1.0]])]});}
            var Q68;
            {var subQ1=sQuery(id+"F4.wireOp",EDGE,"E29.4");var subQ3=sQuery(id+"F4.wireOp",EDGE,"E32");var subQ4=makeQuery(id+"F4.imprint","INTERSECT",VERTEX,{"derivedFrom":[subQ1,subQ3]});Q68=makeQuery(id+"F4.imprint","IMPRINT",FACE,{"disambiguationData":[TD([[makeQuery(id+"F4.imprint","IMPRINT",EDGE,{"disambiguationData":[TD([[subQ4,-1.0]])],"derivedFrom":subQ3}),1.0]])]});}
            var Q69;
            {var subQ0=sQuery(id+"F4.wireOp",EDGE,"E12");var subQ2=sQuery(id+"F4.wireOp",EDGE,"E32");var subQ3=makeQuery(id+"F4.imprint","INTERSECT",VERTEX,{"disambiguationData":[OD(0.0)],"derivedFrom":[subQ0,subQ2]});Q69=makeQuery(id+"F4.imprint","IMPRINT",FACE,{"disambiguationData":[TD([[makeQuery(id+"F4.imprint","IMPRINT",EDGE,{"disambiguationData":[TD([[subQ3,-1.0]])],"derivedFrom":subQ2}),1.0]])]});}
            var Q70;
            {var subQ1=sQuery(id+"F4.wireOp",EDGE,"E12");var subQ3=sQuery(id+"F4.wireOp",EDGE,"E32");var subQ4=makeQuery(id+"F4.imprint","INTERSECT",VERTEX,{"disambiguationData":[OD(0.0)],"derivedFrom":[subQ1,subQ3]});Q70=makeQuery(id+"F4.imprint","IMPRINT",FACE,{"disambiguationData":[TD([[makeQuery(id+"F4.imprint","IMPRINT",EDGE,{"disambiguationData":[TD([[subQ4,1.0]])],"derivedFrom":subQ3}),1.0]])]});}
            var Q71;
            {var subQ1=sQuery(id+"F4.wireOp",EDGE,"E12");var subQ3=sQuery(id+"F4.wireOp",EDGE,"E32");var subQ4=makeQuery(id+"F4.imprint","INTERSECT",VERTEX,{"disambiguationData":[OD(1.0)],"derivedFrom":[subQ1,subQ3]});Q71=makeQuery(id+"F4.imprint","IMPRINT",FACE,{"disambiguationData":[TD([[makeQuery(id+"F4.imprint","IMPRINT",EDGE,{"disambiguationData":[TD([[subQ4,-1.0]])],"derivedFrom":subQ3}),1.0]])]});}
            var Q72;
            {var subQ1=sQuery(id+"F4.wireOp",EDGE,"E29.5");var subQ3=sQuery(id+"F4.wireOp",EDGE,"E31");var subQ4=makeQuery(id+"F4.imprint","INTERSECT",VERTEX,{"derivedFrom":[subQ1,subQ3]});Q72=makeQuery(id+"F4.imprint","IMPRINT",FACE,{"disambiguationData":[TD([[makeQuery(id+"F4.imprint","IMPRINT",EDGE,{"disambiguationData":[TD([[subQ4,-1.0]])],"derivedFrom":subQ3}),1.0]])]});}
            var Q73;
            {var subQ0=sQuery(id+"F4.wireOp",EDGE,"E12");var subQ2=sQuery(id+"F4.wireOp",EDGE,"E31");var subQ3=makeQuery(id+"F4.imprint","INTERSECT",VERTEX,{"disambiguationData":[OD(0.0)],"derivedFrom":[subQ0,subQ2]});Q73=makeQuery(id+"F4.imprint","IMPRINT",FACE,{"disambiguationData":[TD([[makeQuery(id+"F4.imprint","IMPRINT",EDGE,{"disambiguationData":[TD([[subQ3,-1.0]])],"derivedFrom":subQ2}),1.0]])]});}
            var Q74;
            {var subQ1=sQuery(id+"F4.wireOp",EDGE,"E12");var subQ3=sQuery(id+"F4.wireOp",EDGE,"E31");var subQ4=makeQuery(id+"F4.imprint","INTERSECT",VERTEX,{"disambiguationData":[OD(1.0)],"derivedFrom":[subQ1,subQ3]});Q74=makeQuery(id+"F4.imprint","IMPRINT",FACE,{"disambiguationData":[TD([[makeQuery(id+"F4.imprint","IMPRINT",EDGE,{"disambiguationData":[TD([[subQ4,-1.0]])],"derivedFrom":subQ3}),1.0]])]});}
            var Q75;
            {var subQ0=sQuery(id+"F4.wireOp",EDGE,"E12");var subQ2=sQuery(id+"F4.wireOp",EDGE,"E36");var subQ3=makeQuery(id+"F4.imprint","INTERSECT",VERTEX,{"disambiguationData":[OD(0.0)],"derivedFrom":[subQ0,subQ2]});Q75=makeQuery(id+"F4.imprint","IMPRINT",FACE,{"disambiguationData":[TD([[makeQuery(id+"F4.imprint","IMPRINT",EDGE,{"disambiguationData":[TD([[subQ3,-1.0]])],"derivedFrom":subQ2}),1.0]])]});}
            var Q76;
            {var subQ1=sQuery(id+"F4.wireOp",EDGE,"E29.0");var subQ3=sQuery(id+"F4.wireOp",EDGE,"E36");var subQ4=makeQuery(id+"F4.imprint","INTERSECT",VERTEX,{"derivedFrom":[subQ1,subQ3]});Q76=makeQuery(id+"F4.imprint","IMPRINT",FACE,{"disambiguationData":[TD([[makeQuery(id+"F4.imprint","IMPRINT",EDGE,{"disambiguationData":[TD([[subQ4,-1.0]])],"derivedFrom":subQ3}),1.0]])]});}
            var Q77;
            {var subQ1=sQuery(id+"F4.wireOp",EDGE,"E12");var subQ3=sQuery(id+"F4.wireOp",EDGE,"E36");var subQ4=makeQuery(id+"F4.imprint","INTERSECT",VERTEX,{"disambiguationData":[OD(0.0)],"derivedFrom":[subQ1,subQ3]});Q77=makeQuery(id+"F4.imprint","IMPRINT",FACE,{"disambiguationData":[TD([[makeQuery(id+"F4.imprint","IMPRINT",EDGE,{"disambiguationData":[TD([[subQ4,1.0]])],"derivedFrom":subQ3}),1.0]])]});}
            var Q78;
            {var subQ1=sQuery(id+"F4.wireOp",EDGE,"E12");var subQ3=sQuery(id+"F4.wireOp",EDGE,"E36");var subQ4=makeQuery(id+"F4.imprint","INTERSECT",VERTEX,{"disambiguationData":[OD(1.0)],"derivedFrom":[subQ1,subQ3]});Q78=makeQuery(id+"F4.imprint","IMPRINT",FACE,{"disambiguationData":[TD([[makeQuery(id+"F4.imprint","IMPRINT",EDGE,{"disambiguationData":[TD([[subQ4,-1.0]])],"derivedFrom":subQ3}),1.0]])]});}
            var Q79;
            {var subQ0=sQuery(id+"F4.wireOp",EDGE,"E12");var subQ2=sQuery(id+"F4.wireOp",EDGE,"E37");var subQ3=makeQuery(id+"F4.imprint","INTERSECT",VERTEX,{"disambiguationData":[OD(0.0)],"derivedFrom":[subQ0,subQ2]});Q79=makeQuery(id+"F4.imprint","IMPRINT",FACE,{"disambiguationData":[TD([[makeQuery(id+"F4.imprint","IMPRINT",EDGE,{"disambiguationData":[TD([[subQ3,1.0]])],"derivedFrom":subQ2}),1.0]])]});}
            var Q80;
            {var subQ1=sQuery(id+"F4.wireOp",EDGE,"E29.0");var subQ3=sQuery(id+"F4.wireOp",EDGE,"E37");var subQ4=makeQuery(id+"F4.imprint","INTERSECT",VERTEX,{"derivedFrom":[subQ1,subQ3]});Q80=makeQuery(id+"F4.imprint","IMPRINT",FACE,{"disambiguationData":[TD([[makeQuery(id+"F4.imprint","IMPRINT",EDGE,{"disambiguationData":[TD([[subQ4,1.0]])],"derivedFrom":subQ3}),1.0]])]});}
            var Q81;
            {var subQ1=sQuery(id+"F4.wireOp",EDGE,"E12");var subQ3=sQuery(id+"F4.wireOp",EDGE,"E37");var subQ4=makeQuery(id+"F4.imprint","INTERSECT",VERTEX,{"disambiguationData":[OD(0.0)],"derivedFrom":[subQ1,subQ3]});Q81=makeQuery(id+"F4.imprint","IMPRINT",FACE,{"disambiguationData":[TD([[makeQuery(id+"F4.imprint","IMPRINT",EDGE,{"disambiguationData":[TD([[subQ4,-1.0]])],"derivedFrom":subQ3}),1.0]])]});}
            var Q82;
            {var subQ1=sQuery(id+"F4.wireOp",EDGE,"E12");var subQ3=sQuery(id+"F4.wireOp",EDGE,"E37");var subQ4=makeQuery(id+"F4.imprint","INTERSECT",VERTEX,{"disambiguationData":[OD(1.0)],"derivedFrom":[subQ1,subQ3]});Q82=makeQuery(id+"F4.imprint","IMPRINT",FACE,{"disambiguationData":[TD([[makeQuery(id+"F4.imprint","IMPRINT",EDGE,{"disambiguationData":[TD([[subQ4,1.0]])],"derivedFrom":subQ3}),1.0]])]});}
            var Q83;
            {var subQ0=sQuery(id+"F4.wireOp",EDGE,"E12");var subQ2=sQuery(id+"F4.wireOp",EDGE,"E38");var subQ3=makeQuery(id+"F4.imprint","INTERSECT",VERTEX,{"disambiguationData":[OD(0.0)],"derivedFrom":[subQ0,subQ2]});Q83=makeQuery(id+"F4.imprint","IMPRINT",FACE,{"disambiguationData":[TD([[makeQuery(id+"F4.imprint","IMPRINT",EDGE,{"disambiguationData":[TD([[subQ3,-1.0]])],"derivedFrom":subQ2}),1.0]])]});}
            var Q84;
            {var subQ1=sQuery(id+"F4.wireOp",EDGE,"E29.8");var subQ3=sQuery(id+"F4.wireOp",EDGE,"E38");var subQ4=makeQuery(id+"F4.imprint","INTERSECT",VERTEX,{"derivedFrom":[subQ1,subQ3]});Q84=makeQuery(id+"F4.imprint","IMPRINT",FACE,{"disambiguationData":[TD([[makeQuery(id+"F4.imprint","IMPRINT",EDGE,{"disambiguationData":[TD([[subQ4,-1.0]])],"derivedFrom":subQ3}),1.0]])]});}
            var Q85;
            {var subQ1=sQuery(id+"F4.wireOp",EDGE,"E12");var subQ3=sQuery(id+"F4.wireOp",EDGE,"E38");var subQ4=makeQuery(id+"F4.imprint","INTERSECT",VERTEX,{"disambiguationData":[OD(0.0)],"derivedFrom":[subQ1,subQ3]});Q85=makeQuery(id+"F4.imprint","IMPRINT",FACE,{"disambiguationData":[TD([[makeQuery(id+"F4.imprint","IMPRINT",EDGE,{"disambiguationData":[TD([[subQ4,1.0]])],"derivedFrom":subQ3}),1.0]])]});}
            var Q86;
            {var subQ1=sQuery(id+"F4.wireOp",EDGE,"E12");var subQ3=sQuery(id+"F4.wireOp",EDGE,"E34");var subQ4=makeQuery(id+"F4.imprint","INTERSECT",VERTEX,{"disambiguationData":[OD(1.0)],"derivedFrom":[subQ1,subQ3]});Q86=makeQuery(id+"F4.imprint","IMPRINT",FACE,{"disambiguationData":[TD([[makeQuery(id+"F4.imprint","IMPRINT",EDGE,{"disambiguationData":[TD([[subQ4,-1.0]])],"derivedFrom":subQ3}),1.0]])]});}
            var Q87;
            {var subQ1=sQuery(id+"F4.wireOp",EDGE,"E29.7");var subQ3=sQuery(id+"F4.wireOp",EDGE,"E39");var subQ4=makeQuery(id+"F4.imprint","INTERSECT",VERTEX,{"derivedFrom":[subQ1,subQ3]});Q87=makeQuery(id+"F4.imprint","IMPRINT",FACE,{"disambiguationData":[TD([[makeQuery(id+"F4.imprint","IMPRINT",EDGE,{"disambiguationData":[TD([[subQ4,-1.0]])],"derivedFrom":subQ3}),1.0]])]});}
            var Q88;
            {var subQ0=sQuery(id+"F4.wireOp",EDGE,"E12");var subQ2=sQuery(id+"F4.wireOp",EDGE,"E39");var subQ3=makeQuery(id+"F4.imprint","INTERSECT",VERTEX,{"disambiguationData":[OD(0.0)],"derivedFrom":[subQ0,subQ2]});Q88=makeQuery(id+"F4.imprint","IMPRINT",FACE,{"disambiguationData":[TD([[makeQuery(id+"F4.imprint","IMPRINT",EDGE,{"disambiguationData":[TD([[subQ3,-1.0]])],"derivedFrom":subQ2}),1.0]])]});}
            var Q89;
            {var subQ1=sQuery(id+"F4.wireOp",EDGE,"E29.6");var subQ3=sQuery(id+"F4.wireOp",EDGE,"E30");var subQ4=makeQuery(id+"F4.imprint","INTERSECT",VERTEX,{"derivedFrom":[subQ1,subQ3]});Q89=makeQuery(id+"F4.imprint","IMPRINT",FACE,{"disambiguationData":[TD([[makeQuery(id+"F4.imprint","IMPRINT",EDGE,{"disambiguationData":[TD([[subQ4,-1.0]])],"derivedFrom":subQ3}),1.0]])]});}
            var Q90;
            {var subQ0=sQuery(id+"F4.wireOp",EDGE,"E12");var subQ2=sQuery(id+"F4.wireOp",EDGE,"E30");var subQ3=makeQuery(id+"F4.imprint","INTERSECT",VERTEX,{"disambiguationData":[OD(0.0)],"derivedFrom":[subQ0,subQ2]});Q90=makeQuery(id+"F4.imprint","IMPRINT",FACE,{"disambiguationData":[TD([[makeQuery(id+"F4.imprint","IMPRINT",EDGE,{"disambiguationData":[TD([[subQ3,-1.0]])],"derivedFrom":subQ2}),1.0]])]});}
            var Q91;
            {var subQ1=sQuery(id+"F4.wireOp",EDGE,"E12");var subQ3=sQuery(id+"F4.wireOp",EDGE,"E31");var subQ4=makeQuery(id+"F4.imprint","INTERSECT",VERTEX,{"disambiguationData":[OD(0.0)],"derivedFrom":[subQ1,subQ3]});Q91=makeQuery(id+"F4.imprint","IMPRINT",FACE,{"disambiguationData":[TD([[makeQuery(id+"F4.imprint","IMPRINT",EDGE,{"disambiguationData":[TD([[subQ4,1.0]])],"derivedFrom":subQ3}),1.0]])]});}
            var Q92;
            {var subQ1=sQuery(id+"F4.wireOp",EDGE,"E12");var subQ3=sQuery(id+"F4.wireOp",EDGE,"E30");var subQ4=makeQuery(id+"F4.imprint","INTERSECT",VERTEX,{"disambiguationData":[OD(1.0)],"derivedFrom":[subQ1,subQ3]});Q92=makeQuery(id+"F4.imprint","IMPRINT",FACE,{"disambiguationData":[TD([[makeQuery(id+"F4.imprint","IMPRINT",EDGE,{"disambiguationData":[TD([[subQ4,-1.0]])],"derivedFrom":subQ3}),1.0]])]});}
            var Q93;
            {var subQ1=sQuery(id+"F4.wireOp",EDGE,"E12");var subQ3=sQuery(id+"F4.wireOp",EDGE,"E30");var subQ4=makeQuery(id+"F4.imprint","INTERSECT",VERTEX,{"disambiguationData":[OD(0.0)],"derivedFrom":[subQ1,subQ3]});Q93=makeQuery(id+"F4.imprint","IMPRINT",FACE,{"disambiguationData":[TD([[makeQuery(id+"F4.imprint","IMPRINT",EDGE,{"disambiguationData":[TD([[subQ4,1.0]])],"derivedFrom":subQ3}),1.0]])]});}
            var Q94;
            {var subQ1=sQuery(id+"F4.wireOp",EDGE,"E12");var subQ3=sQuery(id+"F4.wireOp",EDGE,"E39");var subQ4=makeQuery(id+"F4.imprint","INTERSECT",VERTEX,{"disambiguationData":[OD(1.0)],"derivedFrom":[subQ1,subQ3]});Q94=makeQuery(id+"F4.imprint","IMPRINT",FACE,{"disambiguationData":[TD([[makeQuery(id+"F4.imprint","IMPRINT",EDGE,{"disambiguationData":[TD([[subQ4,-1.0]])],"derivedFrom":subQ3}),1.0]])]});}
            var Q95;
            {var subQ1=sQuery(id+"F4.wireOp",EDGE,"E12");var subQ3=sQuery(id+"F4.wireOp",EDGE,"E39");var subQ4=makeQuery(id+"F4.imprint","INTERSECT",VERTEX,{"disambiguationData":[OD(0.0)],"derivedFrom":[subQ1,subQ3]});Q95=makeQuery(id+"F4.imprint","IMPRINT",FACE,{"disambiguationData":[TD([[makeQuery(id+"F4.imprint","IMPRINT",EDGE,{"disambiguationData":[TD([[subQ4,1.0]])],"derivedFrom":subQ3}),1.0]])]});}
            var Q96;
            {var subQ1=sQuery(id+"F4.wireOp",EDGE,"E12");var subQ3=sQuery(id+"F4.wireOp",EDGE,"E38");var subQ4=makeQuery(id+"F4.imprint","INTERSECT",VERTEX,{"disambiguationData":[OD(1.0)],"derivedFrom":[subQ1,subQ3]});Q96=makeQuery(id+"F4.imprint","IMPRINT",FACE,{"disambiguationData":[TD([[makeQuery(id+"F4.imprint","IMPRINT",EDGE,{"disambiguationData":[TD([[subQ4,-1.0]])],"derivedFrom":subQ3}),1.0]])]});}
            extrude(context, id + "F5", {"entities" : qUnion([Q0, Q1, Q2, Q3, Q4, Q5, Q6, Q7, Q8, Q9, Q10, Q11, Q12, Q13, Q14, Q15, Q16, Q17, Q18, Q19, Q20, Q21, Q22, Q23, Q24, Q25, Q26, Q27, Q28, Q29, Q30, Q31, Q32, Q33, Q34, Q35, Q36, Q37, Q38, Q39, Q40, Q41, Q42, Q43, Q44, Q45, Q46, Q47, Q48, Q49, Q50, Q51, Q52, Q53, Q54, Q55, Q56, Q57, Q58, Q59, Q60, Q61, Q62, Q63, Q64, Q65, Q66, Q67, Q68, Q69, Q70, Q71, Q72, Q73, Q74, Q75, Q76, Q77, Q78, Q79, Q80, Q81, Q82, Q83, Q84, Q85, Q86, Q87, Q88, Q89, Q90, Q91, Q92, Q93, Q94, Q95, Q96]), "operationType" : NewBodyOperationType.ADD, "depth" : 7 * mm, "offsetDistance" : 25 * mm});
        }
        {
            var Q0;
            Q0=makeQuery(id+"F5.opExtrude","CAP_EDGE",EDGE,{"disambiguationData":[OSD([sQuery(id+"F4.wireOp",EDGE,"E14")])],"isStart":false});
            var Q1;
            Q1=makeQuery(id+"F5.opExtrude","CAP_EDGE",EDGE,{"disambiguationData":[OSD([sQuery(id+"F4.wireOp",EDGE,"E22")])],"isStart":false});
            var Q2;
            Q2=makeQuery(id+"F5.opExtrude","CAP_FACE",FACE,{"disambiguationData":[OSD([sQuery(id+"F4.wireOp",EDGE,"E23")])],"isStart":false});
            var Q3;
            Q3=makeQuery(id+"F5.opExtrude","CAP_FACE",FACE,{"disambiguationData":[OSD([sQuery(id+"F4.wireOp",EDGE,"E26")])],"isStart":false});
            var Q4;
            Q4=makeQuery(id+"F5.opExtrude","CAP_FACE",FACE,{"disambiguationData":[OSD([sQuery(id+"F4.wireOp",EDGE,"E15")])],"isStart":false});
            var Q5;
            Q5=makeQuery(id+"F5.opExtrude","CAP_EDGE",EDGE,{"disambiguationData":[OSD([sQuery(id+"F4.wireOp",EDGE,"E21")])],"isStart":false});
            var Q6;
            Q6=makeQuery(id+"F5.opExtrude","CAP_EDGE",EDGE,{"disambiguationData":[OSD([sQuery(id+"F4.wireOp",EDGE,"E20")])],"isStart":false});
            var Q7;
            Q7=makeQuery(id+"F5.opExtrude","CAP_EDGE",EDGE,{"disambiguationData":[OSD([sQuery(id+"F4.wireOp",EDGE,"E27")])],"isStart":false});
            var Q8;
            Q8=makeQuery(id+"F5.opExtrude","CAP_EDGE",EDGE,{"disambiguationData":[OSD([sQuery(id+"F4.wireOp",EDGE,"E28")])],"isStart":false});
            var Q9;
            Q9=makeQuery(id+"F5.opExtrude","CAP_EDGE",EDGE,{"disambiguationData":[OSD([sQuery(id+"F4.wireOp",EDGE,"E25")])],"isStart":false});
            var Q10;
            Q10=makeQuery(id+"F5.opExtrude","CAP_EDGE",EDGE,{"disambiguationData":[OSD([sQuery(id+"F4.wireOp",EDGE,"E19")])],"isStart":false});
            var Q11;
            Q11=makeQuery(id+"F5.opExtrude","CAP_EDGE",EDGE,{"disambiguationData":[OSD([sQuery(id+"F4.wireOp",EDGE,"E18")])],"isStart":false});
            var Q12;
            Q12=makeQuery(id+"F5.opExtrude","CAP_EDGE",EDGE,{"disambiguationData":[OSD([sQuery(id+"F4.wireOp",EDGE,"E17")])],"isStart":false});
            var Q13;
            Q13=makeQuery(id+"F5.opExtrude","CAP_EDGE",EDGE,{"disambiguationData":[OSD([sQuery(id+"F4.wireOp",EDGE,"E16")])],"isStart":false});
            var Q14;
            Q14=makeQuery(id+"F5.opExtrude","CAP_EDGE",EDGE,{"disambiguationData":[OSD([sQuery(id+"F4.wireOp",EDGE,"E31")])],"isStart":false});
            var Q15;
            Q15=makeQuery(id+"F5.opExtrude","CAP_EDGE",EDGE,{"disambiguationData":[OSD([sQuery(id+"F4.wireOp",EDGE,"E30")])],"isStart":false});
            var Q16;
            Q16=makeQuery(id+"F5.opExtrude","CAP_EDGE",EDGE,{"disambiguationData":[OSD([sQuery(id+"F4.wireOp",EDGE,"E39")])],"isStart":false});
            var Q17;
            Q17=makeQuery(id+"F5.opExtrude","CAP_EDGE",EDGE,{"disambiguationData":[OSD([sQuery(id+"F4.wireOp",EDGE,"E38")])],"isStart":false});
            var Q18;
            Q18=makeQuery(id+"F5.opExtrude","CAP_EDGE",EDGE,{"disambiguationData":[OSD([sQuery(id+"F4.wireOp",EDGE,"E37")])],"isStart":false});
            var Q19;
            Q19=makeQuery(id+"F5.opExtrude","CAP_EDGE",EDGE,{"disambiguationData":[OSD([sQuery(id+"F4.wireOp",EDGE,"E42")])],"isStart":false});
            var Q20;
            Q20=makeQuery(id+"F5.opExtrude","CAP_EDGE",EDGE,{"disambiguationData":[OSD([sQuery(id+"F4.wireOp",EDGE,"E43")])],"isStart":false});
            var Q21;
            Q21=makeQuery(id+"F5.opExtrude","CAP_EDGE",EDGE,{"disambiguationData":[OSD([sQuery(id+"F4.wireOp",EDGE,"E44")])],"isStart":false});
            var Q22;
            Q22=makeQuery(id+"F5.opExtrude","CAP_EDGE",EDGE,{"disambiguationData":[OSD([sQuery(id+"F4.wireOp",EDGE,"E32")])],"isStart":false});
            var Q23;
            Q23=makeQuery(id+"F5.opExtrude","CAP_EDGE",EDGE,{"disambiguationData":[OSD([sQuery(id+"F4.wireOp",EDGE,"E41")])],"isStart":false});
            var Q24;
            Q24=makeQuery(id+"F5.opExtrude","CAP_EDGE",EDGE,{"disambiguationData":[OSD([sQuery(id+"F4.wireOp",EDGE,"E36")])],"isStart":false});
            var Q25;
            Q25=makeQuery(id+"F5.opExtrude","CAP_EDGE",EDGE,{"disambiguationData":[OSD([sQuery(id+"F4.wireOp",EDGE,"E35")])],"isStart":false});
            var Q26;
            Q26=makeQuery(id+"F5.opExtrude","CAP_EDGE",EDGE,{"disambiguationData":[OSD([sQuery(id+"F4.wireOp",EDGE,"E34")])],"isStart":false});
            var Q27;
            Q27=makeQuery(id+"F5.opExtrude","CAP_EDGE",EDGE,{"disambiguationData":[OSD([sQuery(id+"F4.wireOp",EDGE,"E33")])],"isStart":false});
            fillet(context, id + "F6", {"entities" : qUnion([Q0, Q1, Q2, Q3, Q4, Q5, Q6, Q7, Q8, Q9, Q10, Q11, Q12, Q13, Q14, Q15, Q16, Q17, Q18, Q19, Q20, Q21, Q22, Q23, Q24, Q25, Q26, Q27]), "radius" : .75 * mm, "tangentPropagation" : true, "allowEdgeOverflow" : false});
        }
        {
            var Q0;
            Q0=makeQuery(id+"F4.imprint","IMPRINT",FACE,{"disambiguationData":[TD([[makeQuery(id+"F4.imprint","IMPRINT",EDGE,{"derivedFrom":sQuery(id+"F4.wireOp",EDGE,"E8")}),1.0]])]});
            var Q1;
            Q1=makeQuery(id+"F4.imprint","IMPRINT",FACE,{"disambiguationData":[TD([[makeQuery(id+"F4.imprint","IMPRINT",EDGE,{"derivedFrom":sQuery(id+"F4.wireOp",EDGE,"E7")}),1.0]])]});
            extrude(context, id + "F7", {"entities" : qUnion([Q0, Q1]), "operationType" : NewBodyOperationType.ADD, "depth" : 8 * mm, "offsetDistance" : 25 * mm});
        }
        {
            var Q0;
            Q0=makeQuery(id+"F7.opExtrude","CAP_EDGE",EDGE,{"disambiguationData":[OSD([sQuery(id+"F4.wireOp",EDGE,"E8")])],"isStart":false});
            var Q1;
            Q1=makeQuery(id+"F7.opExtrude","CAP_EDGE",EDGE,{"disambiguationData":[OSD([sQuery(id+"F4.wireOp",EDGE,"E9")])],"isStart":false});
            var Q2;
            Q2=makeQuery(id+"F7.opExtrude","CAP_EDGE",EDGE,{"disambiguationData":[OSD([sQuery(id+"F4.wireOp",EDGE,"E7")])],"isStart":false});
            var Q3;
            Q3=makeQuery(id+"F7.opExtrude","CAP_EDGE",EDGE,{"disambiguationData":[OSD([sQuery(id+"F4.wireOp",EDGE,"E10")])],"isStart":false});
            fillet(context, id + "F8", {"entities" : qUnion([Q0, Q1, Q2, Q3]), "radius" : .75 * mm, "tangentPropagation" : true, "allowEdgeOverflow" : false});
        }
        {
            var Q0;
            Q0=makeQuery(id+"F4.imprint","IMPRINT",FACE,{"disambiguationData":[TD([[makeQuery(id+"F4.imprint","IMPRINT",EDGE,{"derivedFrom":sQuery(id+"F4.wireOp",EDGE,"E46.bottom")}),-1.0]])]});
            var Q1;
            Q1=makeQuery(id+"F4.imprint","IMPRINT",FACE,{"disambiguationData":[TD([[makeQuery(id+"F4.imprint","IMPRINT",EDGE,{"derivedFrom":sQuery(id+"F4.wireOp",EDGE,"E47.bottom")}),-1.0]])]});
            var Q2;
            Q2=makeQuery(id+"F4.imprint","IMPRINT",FACE,{"disambiguationData":[TD([[makeQuery(id+"F4.imprint","IMPRINT",EDGE,{"derivedFrom":sQuery(id+"F4.wireOp",EDGE,"E48.bottom")}),-1.0]])]});
            var Q3;
            Q3=makeQuery(id+"F4.imprint","IMPRINT",FACE,{"disambiguationData":[TD([[makeQuery(id+"F4.imprint","IMPRINT",EDGE,{"derivedFrom":sQuery(id+"F4.wireOp",EDGE,"E45.bottom")}),-1.0]])]});
            var Q4;
            Q4=makeQuery(id+"F4.imprint","IMPRINT",FACE,{"disambiguationData":[TD([[makeQuery(id+"F4.imprint","IMPRINT",EDGE,{"derivedFrom":sQuery(id+"F4.wireOp",EDGE,"E49.bottom")}),-1.0]])]});
            extrude(context, id + "F9", {"entities" : qUnion([Q0, Q1, Q2, Q3, Q4]), "operationType" : NewBodyOperationType.ADD, "depth" : 22 * mm, "offsetDistance" : 25 * mm});
        }
        {
            var Q0;
            Q0=makeQuery(id+"F9.opExtrude","SWEPT_FACE",FACE,{"disambiguationData":[OSD([sQuery(id+"F4.wireOp",EDGE,"E45.bottom")])]});
            var sketch = newSketch(context, id + "F10", { "sketchPlane" : qUnion([Q0])});
            skCircle(sketch, "E57", {"center": v(-38.79, -102.7) * mm, "radius": 5 * mm});
            skPoint(sketch, "E57.centerSnap0", {"position": v(-38.79, -111) * mm});
            skSolve(sketch);
        }
        {
            var Q0;
            Q0=makeQuery(id+"F9.opExtrude","SWEPT_FACE",FACE,{"disambiguationData":[OSD([sQuery(id+"F4.wireOp",EDGE,"E49.bottom")])]});
            var sketch = newSketch(context, id + "F11", { "sketchPlane" : qUnion([Q0])});
            skCircle(sketch, "E58", {"center": v(2.75, -102.43) * mm, "radius": 5 * mm});
            skPoint(sketch, "E58.centerSnap0", {"position": v(2.75, -111) * mm});
            skSolve(sketch);
        }
        {
            var Q0;
            Q0=makeQuery(id+"F11.imprint","IMPRINT",FACE,{"disambiguationData":[TD([[makeQuery(id+"F11.imprint","IMPRINT",EDGE,{"derivedFrom":sQuery(id+"F11.wireOp",EDGE,"E58")}),1.0]])]});
            var Q1;
            Q1=makeQuery(id+"F10.imprint","IMPRINT",FACE,{"disambiguationData":[TD([[makeQuery(id+"F10.imprint","IMPRINT",EDGE,{"derivedFrom":sQuery(id+"F10.wireOp",EDGE,"E57")}),1.0]])]});
            extrude(context, id + "F12", {"entities" : qUnion([Q0, Q1]), "operationType" : NewBodyOperationType.REMOVE, "oppositeDirection" : true, "depth" : 4 * mm, "offsetDistance" : 25 * mm});
        }
        {
            var Q0;
            Q0=makeQuery(id+"F9.opExtrude","SWEPT_FACE",FACE,{"disambiguationData":[OSD([sQuery(id+"F4.wireOp",EDGE,"E46.left")])]});
            var sketch = newSketch(context, id + "F13", { "sketchPlane" : qUnion([Q0])});
            skCircle(sketch, "E59", {"center": v(104.47, 44.96) * mm, "radius": 4.5 * mm});
            skPoint(sketch, "E59.centerSnap0", {"position": v(111, 44.96) * mm});
            skSolve(sketch);
        }
        {
            var Q0;
            Q0=makeQuery(id+"F9.opExtrude","SWEPT_FACE",FACE,{"disambiguationData":[OSD([sQuery(id+"F4.wireOp",EDGE,"E48.left")])]});
            var sketch = newSketch(context, id + "F14", { "sketchPlane" : qUnion([Q0])});
            skCircle(sketch, "E60", {"center": v(104.4, 22.7) * mm, "radius": 4.5 * mm});
            skPoint(sketch, "E60.centerSnap0", {"position": v(111, 22.7) * mm});
            skSolve(sketch);
        }
        {
            var Q0;
            Q0=makeQuery(id+"F13.imprint","IMPRINT",FACE,{"disambiguationData":[TD([[makeQuery(id+"F13.imprint","IMPRINT",EDGE,{"derivedFrom":sQuery(id+"F13.wireOp",EDGE,"E59")}),1.0]])]});
            var Q1;
            Q1=makeQuery(id+"F14.imprint","IMPRINT",FACE,{"disambiguationData":[TD([[makeQuery(id+"F14.imprint","IMPRINT",EDGE,{"derivedFrom":sQuery(id+"F14.wireOp",EDGE,"E60")}),1.0]])]});
            extrude(context, id + "F15", {"entities" : qUnion([Q0, Q1]), "operationType" : NewBodyOperationType.REMOVE, "oppositeDirection" : true, "depth" : 30.5 * mm, "offsetDistance" : 25 * mm});
        }
        {
            var Q0;
            Q0=makeQuery(id+"F4.imprint","IMPRINT",FACE,{"disambiguationData":[TD([[makeQuery(id+"F4.imprint","IMPRINT",EDGE,{"derivedFrom":sQuery(id+"F4.wireOp",EDGE,"E50.bottom")}),1.0]])]});
            extrude(context, id + "F16", {"entities" : qUnion([Q0]), "operationType" : NewBodyOperationType.ADD, "depth" : 2 * mm, "offsetDistance" : 25 * mm});
        }
        {
            var Q0;
            Q0=makeQuery(id+"F4.imprint","IMPRINT",FACE,{"disambiguationData":[TD([[makeQuery(id+"F4.imprint","IMPRINT",EDGE,{"derivedFrom":sQuery(id+"F4.wireOp",EDGE,"E51")}),-1.0]])]});
            extrude(context, id + "F17", {"entities" : qUnion([Q0]), "operationType" : NewBodyOperationType.ADD, "depth" : 8 * mm, "offsetDistance" : 25 * mm});
        }
        {
            var Q0;
            Q0=makeQuery(id+"F16.opExtrude","CAP_EDGE",EDGE,{"disambiguationData":[OSD([sQuery(id+"F4.wireOp",EDGE,"E55")])],"isStart":false});
            var Q1;
            Q1=makeQuery(id+"F16.opExtrude","CAP_EDGE",EDGE,{"disambiguationData":[OSD([sQuery(id+"F4.wireOp",EDGE,"E56")])],"isStart":false});
            fillet(context, id + "F18", {"entities" : qUnion([Q0, Q1]), "radius" : .3 * mm, "tangentPropagation" : true, "allowEdgeOverflow" : false});
        }
        {
            var Q0;
            Q0=makeQuery(id+"F16.opExtrude","CAP_EDGE",EDGE,{"disambiguationData":[OSD([sQuery(id+"F4.wireOp",EDGE,"E50.bottom")])],"isStart":false});
            var Q1;
            Q1=makeQuery(id+"F16.opExtrude","CAP_EDGE",EDGE,{"disambiguationData":[OSD([sQuery(id+"F4.wireOp",EDGE,"E50.left")])],"isStart":false});
            var Q2;
            Q2=makeQuery(id+"F16.opExtrude","SWEPT_EDGE",EDGE,{"disambiguationData":[OSD([sQuery(id+"F4.wireOp",EDGE,"E50.bottom"),sQuery(id+"F4.wireOp",EDGE,"E50.left")])]});
            var Q3;
            Q3=makeQuery(id+"F16.opExtrude","SWEPT_EDGE",EDGE,{"disambiguationData":[OSD([sQuery(id+"F4.wireOp",EDGE,"E50.bottom"),sQuery(id+"F4.wireOp",EDGE,"E50.right")])]});
            var Q4;
            Q4=makeQuery(id+"F16.opExtrude","CAP_EDGE",EDGE,{"disambiguationData":[OSD([sQuery(id+"F4.wireOp",EDGE,"E50.right")])],"isStart":false});
            var Q5;
            Q5=makeQuery(id+"F16.opExtrude","SWEPT_EDGE",EDGE,{"disambiguationData":[OSD([sQuery(id+"F4.wireOp",EDGE,"E50.top"),sQuery(id+"F4.wireOp",EDGE,"E50.right")])]});
            var Q6;
            Q6=makeQuery(id+"F16.opExtrude","CAP_EDGE",EDGE,{"disambiguationData":[OSD([sQuery(id+"F4.wireOp",EDGE,"E50.top")])],"isStart":false});
            var Q7;
            Q7=makeQuery(id+"F16.opExtrude","SWEPT_EDGE",EDGE,{"disambiguationData":[OSD([sQuery(id+"F4.wireOp",EDGE,"E50.top"),sQuery(id+"F4.wireOp",EDGE,"E50.left")])]});
            var Q8;
            Q8=makeQuery(id+"F17.opExtrude","CAP_EDGE",EDGE,{"disambiguationData":[OSD([sQuery(id+"F4.wireOp",EDGE,"E52")])],"isStart":false});
            var Q9;
            Q9=makeQuery(id+"F17.opExtrude","CAP_EDGE",EDGE,{"disambiguationData":[OSD([sQuery(id+"F4.wireOp",EDGE,"E54")])],"isStart":false});
            var Q10;
            Q10=makeQuery(id+"F17.opExtrude","SWEPT_EDGE",EDGE,{"disambiguationData":[OSD([sQuery(id+"F4.wireOp",EDGE,"E52"),sQuery(id+"F4.wireOp",EDGE,"E54")])]});
            var Q11;
            Q11=makeQuery(id+"F17.opExtrude","SWEPT_EDGE",EDGE,{"disambiguationData":[OSD([sQuery(id+"F4.wireOp",EDGE,"E52"),sQuery(id+"F4.wireOp",EDGE,"E53")])]});
            var Q12;
            Q12=makeQuery(id+"F17.opExtrude","SWEPT_EDGE",EDGE,{"disambiguationData":[OSD([sQuery(id+"F4.wireOp",EDGE,"E51"),sQuery(id+"F4.wireOp",EDGE,"E53")])]});
            var Q13;
            Q13=makeQuery(id+"F17.opExtrude","CAP_EDGE",EDGE,{"disambiguationData":[OSD([sQuery(id+"F4.wireOp",EDGE,"E53")])],"isStart":false});
            var Q14;
            Q14=makeQuery(id+"F17.opExtrude","SWEPT_EDGE",EDGE,{"disambiguationData":[OSD([sQuery(id+"F4.wireOp",EDGE,"E51"),sQuery(id+"F4.wireOp",EDGE,"E54")])]});
            var Q15;
            Q15=makeQuery(id+"F17.opExtrude","CAP_EDGE",EDGE,{"disambiguationData":[OSD([sQuery(id+"F4.wireOp",EDGE,"E51")])],"isStart":false});
            fillet(context, id + "F19", {"entities" : qUnion([Q0, Q1, Q2, Q3, Q4, Q5, Q6, Q7, Q8, Q9, Q10, Q11, Q12, Q13, Q14, Q15]), "radius" : 1 * mm, "tangentPropagation" : true, "allowEdgeOverflow" : false});
        }
    });
